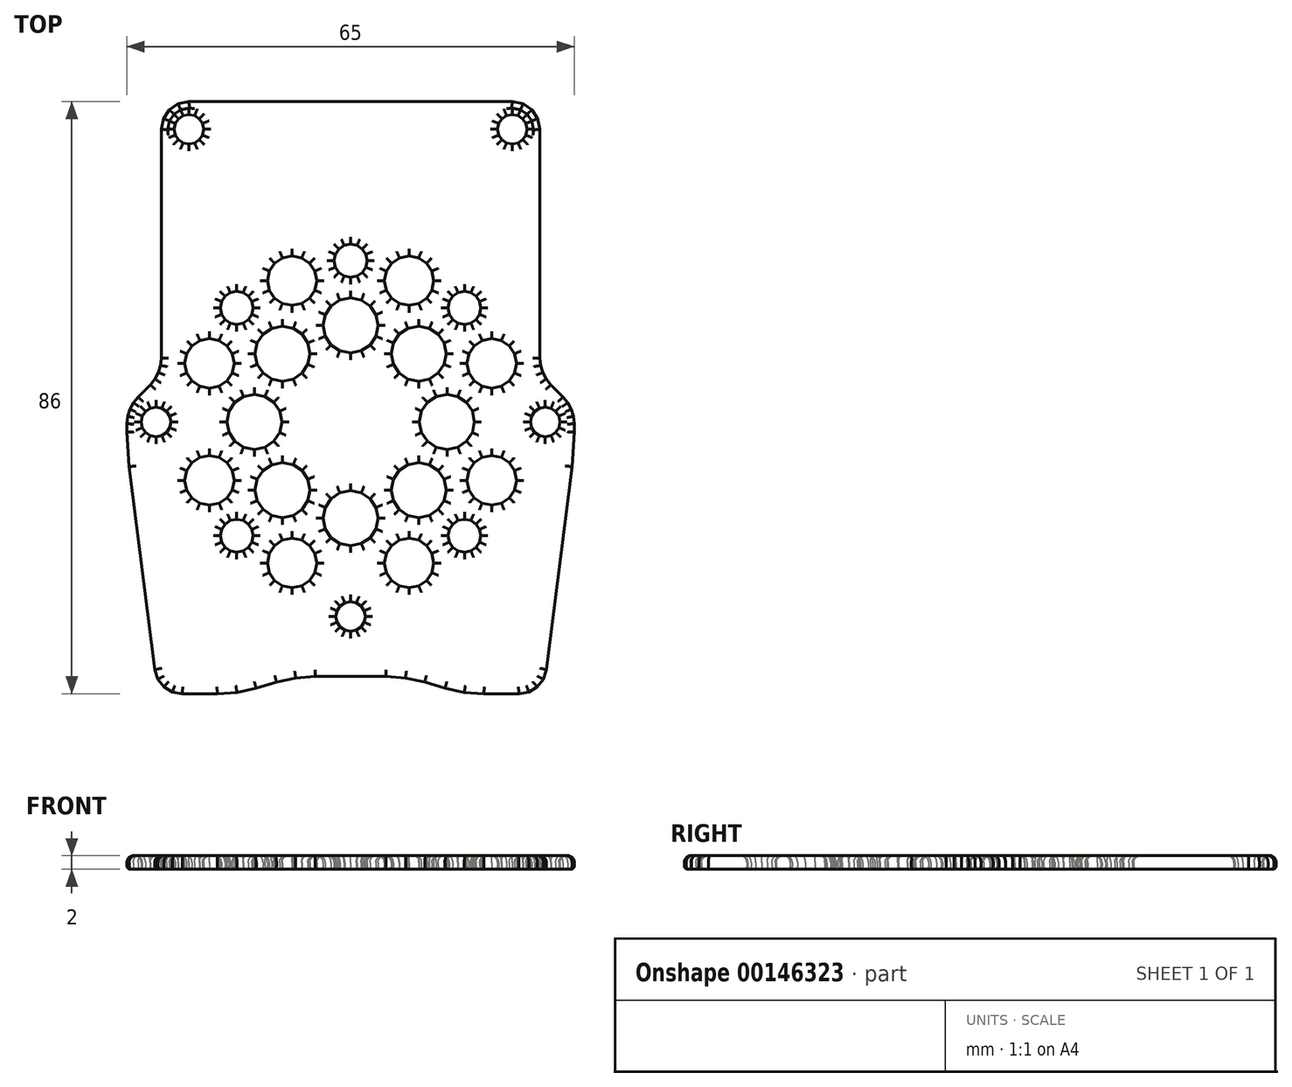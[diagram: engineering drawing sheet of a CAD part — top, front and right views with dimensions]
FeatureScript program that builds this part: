
annotation { "Feature Type Name" : "Feature", "Feature Type Description" : "" }
export const myFeature = defineFeature(function(context is Context, id is Id, definition is map)
    precondition{}
    {
        {
            var Q0;
            Q0=qCreatedBy(makeId("Top.planeOp"),FACE);
            var sketch = newSketch(context, id + "F0", { "sketchPlane" : qUnion([Q0])});
            skLineSegment(sketch, "E0", {"start": v(32.5, -1.28) * mm, "end": v(32.5, -2.48) * mm});
            skLineSegment(sketch, "E1", {"start": v(32.18, -7.5) * mm, "end": v(32.5, -2.48) * mm});
            skLineSegment(sketch, "E2", {"start": v(32.18, -7.5) * mm, "end": v(28.44, -37) * mm});
            skLineSegment(sketch, "E3", {"start": v(24.47, -40.5) * mm, "end": v(25.9, -40.23) * mm});
            skLineSegment(sketch, "E4", {"start": v(25.9, -40.23) * mm, "end": v(27.12, -39.5) * mm});
            skLineSegment(sketch, "E5", {"start": v(27.12, -39.5) * mm, "end": v(28, -38.4) * mm});
            skLineSegment(sketch, "E6", {"start": v(28, -38.4) * mm, "end": v(28.44, -37) * mm});
            skLineSegment(sketch, "E7", {"start": v(-10.76, -38.81) * mm, "end": v(-13.74, -39.69) * mm});
            skLineSegment(sketch, "E8", {"start": v(-19.38, -40.5) * mm, "end": v(-16.53, -40.3) * mm});
            skLineSegment(sketch, "E9", {"start": v(-16.53, -40.3) * mm, "end": v(-13.74, -39.69) * mm});
            skLineSegment(sketch, "E10", {"start": v(-19.38, -40.5) * mm, "end": v(-24.48, -40.5) * mm});
            skLineSegment(sketch, "E11", {"start": v(-5.12, -38) * mm, "end": v(-7.97, -38.2) * mm});
            skLineSegment(sketch, "E12", {"start": v(-7.97, -38.2) * mm, "end": v(-10.76, -38.81) * mm});
            skLineSegment(sketch, "E13", {"start": v(-5.12, -38) * mm, "end": v(5.12, -38) * mm});
            skLineSegment(sketch, "E14", {"start": v(10.76, -38.81) * mm, "end": v(7.97, -38.2) * mm});
            skLineSegment(sketch, "E15", {"start": v(7.97, -38.2) * mm, "end": v(5.12, -38) * mm});
            skLineSegment(sketch, "E16", {"start": v(10.76, -38.81) * mm, "end": v(13.74, -39.69) * mm});
            skLineSegment(sketch, "E17", {"start": v(13.74, -39.69) * mm, "end": v(16.53, -40.3) * mm});
            skLineSegment(sketch, "E18", {"start": v(16.53, -40.3) * mm, "end": v(19.38, -40.5) * mm});
            skLineSegment(sketch, "E19", {"start": v(19.38, -40.5) * mm, "end": v(24.47, -40.5) * mm});
            skLineSegment(sketch, "E20", {"start": v(-28.44, -37) * mm, "end": v(-28, -38.4) * mm});
            skLineSegment(sketch, "E21", {"start": v(-28, -38.4) * mm, "end": v(-27.12, -39.5) * mm});
            skLineSegment(sketch, "E22", {"start": v(-27.12, -39.5) * mm, "end": v(-25.91, -40.23) * mm});
            skLineSegment(sketch, "E23", {"start": v(-25.91, -40.23) * mm, "end": v(-24.48, -40.5) * mm});
            skLineSegment(sketch, "E24", {"start": v(-28.44, -37) * mm, "end": v(-32.18, -7.5) * mm});
            skLineSegment(sketch, "E25", {"start": v(-32.5, -2.48) * mm, "end": v(-32.18, -7.5) * mm});
            skLineSegment(sketch, "E26", {"start": v(-32.5, -2.48) * mm, "end": v(-32.5, -1.28) * mm});
            skLineSegment(sketch, "E27", {"start": v(-23.5, 45.5) * mm, "end": v(23.5, 45.5) * mm});
            skLineSegment(sketch, "E28", {"start": v(27.5, 41.5) * mm, "end": v(27.18, 43.06) * mm});
            skLineSegment(sketch, "E29", {"start": v(27.18, 43.06) * mm, "end": v(26.33, 44.33) * mm});
            skLineSegment(sketch, "E30", {"start": v(26.33, 44.33) * mm, "end": v(25.05, 45.19) * mm});
            skLineSegment(sketch, "E31", {"start": v(25.05, 45.19) * mm, "end": v(23.5, 45.5) * mm});
            skLineSegment(sketch, "E32", {"start": v(27.5, 41.5) * mm, "end": v(27.5, 8.28) * mm});
            skLineSegment(sketch, "E33", {"start": v(27.5, 8.28) * mm, "end": v(27.6, 7.2) * mm});
            skLineSegment(sketch, "E34", {"start": v(27.6, 7.2) * mm, "end": v(27.92, 6.17) * mm});
            skLineSegment(sketch, "E35", {"start": v(27.92, 6.17) * mm, "end": v(28.42, 5.23) * mm});
            skLineSegment(sketch, "E36", {"start": v(28.42, 5.23) * mm, "end": v(29.11, 4.39) * mm});
            skLineSegment(sketch, "E37", {"start": v(29.11, 4.39) * mm, "end": v(30.89, 2.61) * mm});
            skLineSegment(sketch, "E38", {"start": v(32.5, -1.28) * mm, "end": v(32.4, -0.2) * mm});
            skLineSegment(sketch, "E39", {"start": v(32.4, -0.2) * mm, "end": v(32.08, 0.83) * mm});
            skLineSegment(sketch, "E40", {"start": v(32.08, 0.83) * mm, "end": v(31.57, 1.77) * mm});
            skLineSegment(sketch, "E41", {"start": v(31.57, 1.77) * mm, "end": v(30.89, 2.61) * mm});
            skLineSegment(sketch, "E42", {"start": v(-30.89, 2.61) * mm, "end": v(-31.58, 1.77) * mm});
            skLineSegment(sketch, "E43", {"start": v(-31.58, 1.77) * mm, "end": v(-32.08, 0.83) * mm});
            skLineSegment(sketch, "E44", {"start": v(-32.08, 0.83) * mm, "end": v(-32.4, -0.2) * mm});
            skLineSegment(sketch, "E45", {"start": v(-32.4, -0.2) * mm, "end": v(-32.5, -1.28) * mm});
            skLineSegment(sketch, "E46", {"start": v(-30.89, 2.61) * mm, "end": v(-29.11, 4.39) * mm});
            skLineSegment(sketch, "E47", {"start": v(-29.11, 4.39) * mm, "end": v(-28.43, 5.23) * mm});
            skLineSegment(sketch, "E48", {"start": v(-28.43, 5.23) * mm, "end": v(-27.92, 6.17) * mm});
            skLineSegment(sketch, "E49", {"start": v(-27.92, 6.17) * mm, "end": v(-27.6, 7.2) * mm});
            skLineSegment(sketch, "E50", {"start": v(-27.6, 7.2) * mm, "end": v(-27.5, 8.28) * mm});
            skLineSegment(sketch, "E51", {"start": v(-27.5, 8.28) * mm, "end": v(-27.5, 41.5) * mm});
            skLineSegment(sketch, "E52", {"start": v(-23.5, 45.5) * mm, "end": v(-25.06, 45.19) * mm});
            skLineSegment(sketch, "E53", {"start": v(-25.06, 45.19) * mm, "end": v(-26.33, 44.33) * mm});
            skLineSegment(sketch, "E54", {"start": v(-26.33, 44.33) * mm, "end": v(-27.19, 43.06) * mm});
            skLineSegment(sketch, "E55", {"start": v(-27.19, 43.06) * mm, "end": v(-27.5, 41.5) * mm});
            skLineSegment(sketch, "E56", {"start": v(-26.13, -1) * mm, "end": v(-26.3, -0.16) * mm});
            skLineSegment(sketch, "E57", {"start": v(-26.3, -0.16) * mm, "end": v(-26.76, 0.52) * mm});
            skLineSegment(sketch, "E58", {"start": v(-26.76, 0.52) * mm, "end": v(-27.44, 0.98) * mm});
            skLineSegment(sketch, "E59", {"start": v(-27.44, 0.98) * mm, "end": v(-28.28, 1.15) * mm});
            skLineSegment(sketch, "E60", {"start": v(-28.28, 1.15) * mm, "end": v(-29.12, 0.98) * mm});
            skLineSegment(sketch, "E61", {"start": v(-29.12, 0.98) * mm, "end": v(-29.8, 0.52) * mm});
            skLineSegment(sketch, "E62", {"start": v(-29.8, 0.52) * mm, "end": v(-30.26, -0.16) * mm});
            skLineSegment(sketch, "E63", {"start": v(-30.26, -0.16) * mm, "end": v(-30.43, -1) * mm});
            skLineSegment(sketch, "E64", {"start": v(-30.43, -1) * mm, "end": v(-30.26, -1.83) * mm});
            skLineSegment(sketch, "E65", {"start": v(-30.26, -1.83) * mm, "end": v(-29.8, -2.52) * mm});
            skLineSegment(sketch, "E66", {"start": v(-29.8, -2.52) * mm, "end": v(-29.12, -2.98) * mm});
            skLineSegment(sketch, "E67", {"start": v(-29.12, -2.98) * mm, "end": v(-28.28, -3.15) * mm});
            skLineSegment(sketch, "E68", {"start": v(-28.28, -3.15) * mm, "end": v(-27.44, -2.98) * mm});
            skLineSegment(sketch, "E69", {"start": v(-27.44, -2.98) * mm, "end": v(-26.76, -2.52) * mm});
            skLineSegment(sketch, "E70", {"start": v(-26.76, -2.52) * mm, "end": v(-26.3, -1.83) * mm});
            skLineSegment(sketch, "E71", {"start": v(-26.3, -1.83) * mm, "end": v(-26.13, -1) * mm});
            skLineSegment(sketch, "E72", {"start": v(30.43, -1) * mm, "end": v(30.26, -0.16) * mm});
            skLineSegment(sketch, "E73", {"start": v(30.26, -0.16) * mm, "end": v(29.8, 0.52) * mm});
            skLineSegment(sketch, "E74", {"start": v(29.8, 0.52) * mm, "end": v(29.11, 0.98) * mm});
            skLineSegment(sketch, "E75", {"start": v(29.11, 0.98) * mm, "end": v(28.28, 1.15) * mm});
            skLineSegment(sketch, "E76", {"start": v(28.28, 1.15) * mm, "end": v(27.44, 0.98) * mm});
            skLineSegment(sketch, "E77", {"start": v(27.44, 0.98) * mm, "end": v(26.76, 0.52) * mm});
            skLineSegment(sketch, "E78", {"start": v(26.76, 0.52) * mm, "end": v(26.3, -0.16) * mm});
            skLineSegment(sketch, "E79", {"start": v(26.3, -0.16) * mm, "end": v(26.13, -1) * mm});
            skLineSegment(sketch, "E80", {"start": v(26.13, -1) * mm, "end": v(26.3, -1.83) * mm});
            skLineSegment(sketch, "E81", {"start": v(26.3, -1.83) * mm, "end": v(26.76, -2.52) * mm});
            skLineSegment(sketch, "E82", {"start": v(26.76, -2.52) * mm, "end": v(27.44, -2.98) * mm});
            skLineSegment(sketch, "E83", {"start": v(27.44, -2.98) * mm, "end": v(28.28, -3.15) * mm});
            skLineSegment(sketch, "E84", {"start": v(28.28, -3.15) * mm, "end": v(29.11, -2.98) * mm});
            skLineSegment(sketch, "E85", {"start": v(29.11, -2.98) * mm, "end": v(29.8, -2.52) * mm});
            skLineSegment(sketch, "E86", {"start": v(29.8, -2.52) * mm, "end": v(30.26, -1.83) * mm});
            skLineSegment(sketch, "E87", {"start": v(30.26, -1.83) * mm, "end": v(30.43, -1) * mm});
            skLineSegment(sketch, "E88", {"start": v(2.15, -29.28) * mm, "end": v(1.98, -28.44) * mm});
            skLineSegment(sketch, "E89", {"start": v(1.98, -28.44) * mm, "end": v(1.52, -27.76) * mm});
            skLineSegment(sketch, "E90", {"start": v(1.52, -27.76) * mm, "end": v(0.83, -27.3) * mm});
            skLineSegment(sketch, "E91", {"start": v(0.83, -27.3) * mm, "end": v(0, -27.13) * mm});
            skLineSegment(sketch, "E92", {"start": v(0, -27.13) * mm, "end": v(-0.84, -27.3) * mm});
            skLineSegment(sketch, "E93", {"start": v(-0.84, -27.3) * mm, "end": v(-1.52, -27.76) * mm});
            skLineSegment(sketch, "E94", {"start": v(-1.52, -27.76) * mm, "end": v(-1.98, -28.44) * mm});
            skLineSegment(sketch, "E95", {"start": v(-1.98, -28.44) * mm, "end": v(-2.15, -29.28) * mm});
            skLineSegment(sketch, "E96", {"start": v(-2.15, -29.28) * mm, "end": v(-1.98, -30.11) * mm});
            skLineSegment(sketch, "E97", {"start": v(-1.98, -30.11) * mm, "end": v(-1.52, -30.8) * mm});
            skLineSegment(sketch, "E98", {"start": v(-1.52, -30.8) * mm, "end": v(-0.84, -31.26) * mm});
            skLineSegment(sketch, "E99", {"start": v(-0.84, -31.26) * mm, "end": v(0, -31.43) * mm});
            skLineSegment(sketch, "E100", {"start": v(0, -31.43) * mm, "end": v(0.83, -31.26) * mm});
            skLineSegment(sketch, "E101", {"start": v(0.83, -31.26) * mm, "end": v(1.52, -30.8) * mm});
            skLineSegment(sketch, "E102", {"start": v(1.52, -30.8) * mm, "end": v(1.98, -30.11) * mm});
            skLineSegment(sketch, "E103", {"start": v(1.98, -30.11) * mm, "end": v(2.15, -29.28) * mm});
            skLineSegment(sketch, "E104", {"start": v(-21.35, 41.5) * mm, "end": v(-21.52, 42.34) * mm});
            skLineSegment(sketch, "E105", {"start": v(-21.52, 42.34) * mm, "end": v(-21.98, 43.02) * mm});
            skLineSegment(sketch, "E106", {"start": v(-21.98, 43.02) * mm, "end": v(-22.67, 43.48) * mm});
            skLineSegment(sketch, "E107", {"start": v(-22.67, 43.48) * mm, "end": v(-23.5, 43.65) * mm});
            skLineSegment(sketch, "E108", {"start": v(-23.5, 43.65) * mm, "end": v(-24.34, 43.48) * mm});
            skLineSegment(sketch, "E109", {"start": v(-24.34, 43.48) * mm, "end": v(-25.02, 43.02) * mm});
            skLineSegment(sketch, "E110", {"start": v(-25.02, 43.02) * mm, "end": v(-25.48, 42.34) * mm});
            skLineSegment(sketch, "E111", {"start": v(-25.48, 42.34) * mm, "end": v(-25.65, 41.5) * mm});
            skLineSegment(sketch, "E112", {"start": v(-25.65, 41.5) * mm, "end": v(-25.48, 40.67) * mm});
            skLineSegment(sketch, "E113", {"start": v(-25.48, 40.67) * mm, "end": v(-25.02, 39.98) * mm});
            skLineSegment(sketch, "E114", {"start": v(-25.02, 39.98) * mm, "end": v(-24.34, 39.52) * mm});
            skLineSegment(sketch, "E115", {"start": v(-24.34, 39.52) * mm, "end": v(-23.5, 39.35) * mm});
            skLineSegment(sketch, "E116", {"start": v(-23.5, 39.35) * mm, "end": v(-22.67, 39.52) * mm});
            skLineSegment(sketch, "E117", {"start": v(-22.67, 39.52) * mm, "end": v(-21.98, 39.98) * mm});
            skLineSegment(sketch, "E118", {"start": v(-21.98, 39.98) * mm, "end": v(-21.52, 40.67) * mm});
            skLineSegment(sketch, "E119", {"start": v(-21.52, 40.67) * mm, "end": v(-21.35, 41.5) * mm});
            skLineSegment(sketch, "E120", {"start": v(25.65, 41.5) * mm, "end": v(25.48, 42.34) * mm});
            skLineSegment(sketch, "E121", {"start": v(25.48, 42.34) * mm, "end": v(25.02, 43.02) * mm});
            skLineSegment(sketch, "E122", {"start": v(25.02, 43.02) * mm, "end": v(24.34, 43.48) * mm});
            skLineSegment(sketch, "E123", {"start": v(24.34, 43.48) * mm, "end": v(23.5, 43.65) * mm});
            skLineSegment(sketch, "E124", {"start": v(23.5, 43.65) * mm, "end": v(22.66, 43.48) * mm});
            skLineSegment(sketch, "E125", {"start": v(22.66, 43.48) * mm, "end": v(21.98, 43.02) * mm});
            skLineSegment(sketch, "E126", {"start": v(21.98, 43.02) * mm, "end": v(21.52, 42.34) * mm});
            skLineSegment(sketch, "E127", {"start": v(21.52, 42.34) * mm, "end": v(21.35, 41.5) * mm});
            skLineSegment(sketch, "E128", {"start": v(21.35, 41.5) * mm, "end": v(21.52, 40.67) * mm});
            skLineSegment(sketch, "E129", {"start": v(21.52, 40.67) * mm, "end": v(21.98, 39.98) * mm});
            skLineSegment(sketch, "E130", {"start": v(21.98, 39.98) * mm, "end": v(22.66, 39.52) * mm});
            skLineSegment(sketch, "E131", {"start": v(22.66, 39.52) * mm, "end": v(23.5, 39.35) * mm});
            skLineSegment(sketch, "E132", {"start": v(23.5, 39.35) * mm, "end": v(24.34, 39.52) * mm});
            skLineSegment(sketch, "E133", {"start": v(24.34, 39.52) * mm, "end": v(25.02, 39.98) * mm});
            skLineSegment(sketch, "E134", {"start": v(25.02, 39.98) * mm, "end": v(25.48, 40.67) * mm});
            skLineSegment(sketch, "E135", {"start": v(25.48, 40.67) * mm, "end": v(25.65, 41.5) * mm});
            skLineSegment(sketch, "E136", {"start": v(2.4, 22.4) * mm, "end": v(2.2, 23.33) * mm});
            skLineSegment(sketch, "E137", {"start": v(2.2, 23.33) * mm, "end": v(1.7, 24.1) * mm});
            skLineSegment(sketch, "E138", {"start": v(1.7, 24.1) * mm, "end": v(0.93, 24.61) * mm});
            skLineSegment(sketch, "E139", {"start": v(0.93, 24.61) * mm, "end": v(0, 24.8) * mm});
            skLineSegment(sketch, "E140", {"start": v(0, 24.8) * mm, "end": v(-0.93, 24.61) * mm});
            skLineSegment(sketch, "E141", {"start": v(-0.93, 24.61) * mm, "end": v(-1.7, 24.1) * mm});
            skLineSegment(sketch, "E142", {"start": v(-1.7, 24.1) * mm, "end": v(-2.21, 23.33) * mm});
            skLineSegment(sketch, "E143", {"start": v(-2.21, 23.33) * mm, "end": v(-2.4, 22.4) * mm});
            skLineSegment(sketch, "E144", {"start": v(-2.4, 22.4) * mm, "end": v(-2.21, 21.47) * mm});
            skLineSegment(sketch, "E145", {"start": v(-2.21, 21.47) * mm, "end": v(-1.7, 20.7) * mm});
            skLineSegment(sketch, "E146", {"start": v(-1.7, 20.7) * mm, "end": v(-0.93, 20.19) * mm});
            skLineSegment(sketch, "E147", {"start": v(-0.93, 20.19) * mm, "end": v(0, 20) * mm});
            skLineSegment(sketch, "E148", {"start": v(0, 20) * mm, "end": v(0.93, 20.19) * mm});
            skLineSegment(sketch, "E149", {"start": v(0.93, 20.19) * mm, "end": v(1.7, 20.7) * mm});
            skLineSegment(sketch, "E150", {"start": v(1.7, 20.7) * mm, "end": v(2.2, 21.47) * mm});
            skLineSegment(sketch, "E151", {"start": v(2.2, 21.47) * mm, "end": v(2.4, 22.4) * mm});
            skLineSegment(sketch, "E152", {"start": v(4, 13) * mm, "end": v(3.68, 14.56) * mm});
            skLineSegment(sketch, "E153", {"start": v(3.68, 14.56) * mm, "end": v(2.83, 15.83) * mm});
            skLineSegment(sketch, "E154", {"start": v(2.83, 15.83) * mm, "end": v(1.56, 16.69) * mm});
            skLineSegment(sketch, "E155", {"start": v(1.56, 16.69) * mm, "end": v(0, 17) * mm});
            skLineSegment(sketch, "E156", {"start": v(0, 17) * mm, "end": v(-1.56, 16.69) * mm});
            skLineSegment(sketch, "E157", {"start": v(-1.56, 16.69) * mm, "end": v(-2.83, 15.83) * mm});
            skLineSegment(sketch, "E158", {"start": v(-2.83, 15.83) * mm, "end": v(-3.69, 14.56) * mm});
            skLineSegment(sketch, "E159", {"start": v(-3.69, 14.56) * mm, "end": v(-4, 13) * mm});
            skLineSegment(sketch, "E160", {"start": v(-4, 13) * mm, "end": v(-3.69, 11.44) * mm});
            skLineSegment(sketch, "E161", {"start": v(-3.69, 11.44) * mm, "end": v(-2.83, 10.17) * mm});
            skLineSegment(sketch, "E162", {"start": v(-2.83, 10.17) * mm, "end": v(-1.56, 9.31) * mm});
            skLineSegment(sketch, "E163", {"start": v(-1.56, 9.31) * mm, "end": v(0, 9) * mm});
            skLineSegment(sketch, "E164", {"start": v(0, 9) * mm, "end": v(1.56, 9.31) * mm});
            skLineSegment(sketch, "E165", {"start": v(1.56, 9.31) * mm, "end": v(2.83, 10.17) * mm});
            skLineSegment(sketch, "E166", {"start": v(2.83, 10.17) * mm, "end": v(3.68, 11.44) * mm});
            skLineSegment(sketch, "E167", {"start": v(3.68, 11.44) * mm, "end": v(4, 13) * mm});
            skLineSegment(sketch, "E168", {"start": v(-4.9, 19.5) * mm, "end": v(-5.18, 20.91) * mm});
            skLineSegment(sketch, "E169", {"start": v(-5.18, 20.91) * mm, "end": v(-5.95, 22.06) * mm});
            skLineSegment(sketch, "E170", {"start": v(-5.95, 22.06) * mm, "end": v(-7.1, 22.83) * mm});
            skLineSegment(sketch, "E171", {"start": v(-7.1, 22.83) * mm, "end": v(-8.5, 23.11) * mm});
            skLineSegment(sketch, "E172", {"start": v(-8.5, 23.11) * mm, "end": v(-9.9, 22.83) * mm});
            skLineSegment(sketch, "E173", {"start": v(-9.9, 22.83) * mm, "end": v(-11.04, 22.06) * mm});
            skLineSegment(sketch, "E174", {"start": v(-11.04, 22.06) * mm, "end": v(-11.81, 20.91) * mm});
            skLineSegment(sketch, "E175", {"start": v(-11.81, 20.91) * mm, "end": v(-12.1, 19.5) * mm});
            skLineSegment(sketch, "E176", {"start": v(-12.1, 19.5) * mm, "end": v(-11.81, 18.1) * mm});
            skLineSegment(sketch, "E177", {"start": v(-11.81, 18.1) * mm, "end": v(-11.04, 16.97) * mm});
            skLineSegment(sketch, "E178", {"start": v(-11.04, 16.97) * mm, "end": v(-9.9, 16.2) * mm});
            skLineSegment(sketch, "E179", {"start": v(-9.9, 16.2) * mm, "end": v(-8.5, 15.91) * mm});
            skLineSegment(sketch, "E180", {"start": v(-8.5, 15.91) * mm, "end": v(-7.1, 16.2) * mm});
            skLineSegment(sketch, "E181", {"start": v(-7.1, 16.2) * mm, "end": v(-5.95, 16.97) * mm});
            skLineSegment(sketch, "E182", {"start": v(-5.95, 16.97) * mm, "end": v(-5.18, 18.1) * mm});
            skLineSegment(sketch, "E183", {"start": v(-5.18, 18.1) * mm, "end": v(-4.9, 19.5) * mm});
            skLineSegment(sketch, "E184", {"start": v(4, -15) * mm, "end": v(3.68, -13.44) * mm});
            skLineSegment(sketch, "E185", {"start": v(3.68, -13.44) * mm, "end": v(2.83, -12.17) * mm});
            skLineSegment(sketch, "E186", {"start": v(2.83, -12.17) * mm, "end": v(1.56, -11.31) * mm});
            skLineSegment(sketch, "E187", {"start": v(1.56, -11.31) * mm, "end": v(0, -11) * mm});
            skLineSegment(sketch, "E188", {"start": v(0, -11) * mm, "end": v(-1.56, -11.31) * mm});
            skLineSegment(sketch, "E189", {"start": v(-1.56, -11.31) * mm, "end": v(-2.83, -12.17) * mm});
            skLineSegment(sketch, "E190", {"start": v(-2.83, -12.17) * mm, "end": v(-3.69, -13.44) * mm});
            skLineSegment(sketch, "E191", {"start": v(-3.69, -13.44) * mm, "end": v(-4, -15) * mm});
            skLineSegment(sketch, "E192", {"start": v(-4, -15) * mm, "end": v(-3.69, -16.56) * mm});
            skLineSegment(sketch, "E193", {"start": v(-3.69, -16.56) * mm, "end": v(-2.83, -17.83) * mm});
            skLineSegment(sketch, "E194", {"start": v(-2.83, -17.83) * mm, "end": v(-1.56, -18.68) * mm});
            skLineSegment(sketch, "E195", {"start": v(-1.56, -18.68) * mm, "end": v(0, -19) * mm});
            skLineSegment(sketch, "E196", {"start": v(0, -19) * mm, "end": v(1.56, -18.68) * mm});
            skLineSegment(sketch, "E197", {"start": v(1.56, -18.68) * mm, "end": v(2.83, -17.83) * mm});
            skLineSegment(sketch, "E198", {"start": v(2.83, -17.83) * mm, "end": v(3.68, -16.56) * mm});
            skLineSegment(sketch, "E199", {"start": v(3.68, -16.56) * mm, "end": v(4, -15) * mm});
            skLineSegment(sketch, "E200", {"start": v(12.1, -21.51) * mm, "end": v(11.81, -20.1) * mm});
            skLineSegment(sketch, "E201", {"start": v(11.81, -20.1) * mm, "end": v(11.04, -18.96) * mm});
            skLineSegment(sketch, "E202", {"start": v(11.04, -18.96) * mm, "end": v(9.9, -18.2) * mm});
            skLineSegment(sketch, "E203", {"start": v(9.9, -18.2) * mm, "end": v(8.5, -17.9) * mm});
            skLineSegment(sketch, "E204", {"start": v(8.5, -17.9) * mm, "end": v(7.1, -18.2) * mm});
            skLineSegment(sketch, "E205", {"start": v(7.1, -18.2) * mm, "end": v(5.95, -18.96) * mm});
            skLineSegment(sketch, "E206", {"start": v(5.95, -18.96) * mm, "end": v(5.18, -20.1) * mm});
            skLineSegment(sketch, "E207", {"start": v(5.18, -20.1) * mm, "end": v(4.9, -21.51) * mm});
            skLineSegment(sketch, "E208", {"start": v(4.9, -21.51) * mm, "end": v(5.18, -22.91) * mm});
            skLineSegment(sketch, "E209", {"start": v(5.18, -22.91) * mm, "end": v(5.95, -24.05) * mm});
            skLineSegment(sketch, "E210", {"start": v(5.95, -24.05) * mm, "end": v(7.1, -24.83) * mm});
            skLineSegment(sketch, "E211", {"start": v(7.1, -24.83) * mm, "end": v(8.5, -25.1) * mm});
            skLineSegment(sketch, "E212", {"start": v(8.5, -25.1) * mm, "end": v(9.9, -24.83) * mm});
            skLineSegment(sketch, "E213", {"start": v(9.9, -24.83) * mm, "end": v(11.04, -24.05) * mm});
            skLineSegment(sketch, "E214", {"start": v(11.04, -24.05) * mm, "end": v(11.81, -22.91) * mm});
            skLineSegment(sketch, "E215", {"start": v(11.81, -22.91) * mm, "end": v(12.1, -21.51) * mm});
            skLineSegment(sketch, "E216", {"start": v(-10, -1) * mm, "end": v(-10.32, 0.56) * mm});
            skLineSegment(sketch, "E217", {"start": v(-10.32, 0.56) * mm, "end": v(-11.17, 1.83) * mm});
            skLineSegment(sketch, "E218", {"start": v(-11.17, 1.83) * mm, "end": v(-12.44, 2.69) * mm});
            skLineSegment(sketch, "E219", {"start": v(-12.44, 2.69) * mm, "end": v(-14, 3) * mm});
            skLineSegment(sketch, "E220", {"start": v(-14, 3) * mm, "end": v(-15.56, 2.69) * mm});
            skLineSegment(sketch, "E221", {"start": v(-15.56, 2.69) * mm, "end": v(-16.83, 1.83) * mm});
            skLineSegment(sketch, "E222", {"start": v(-16.83, 1.83) * mm, "end": v(-17.69, 0.56) * mm});
            skLineSegment(sketch, "E223", {"start": v(-17.69, 0.56) * mm, "end": v(-18, -1) * mm});
            skLineSegment(sketch, "E224", {"start": v(-18, -1) * mm, "end": v(-17.69, -2.56) * mm});
            skLineSegment(sketch, "E225", {"start": v(-17.69, -2.56) * mm, "end": v(-16.83, -3.83) * mm});
            skLineSegment(sketch, "E226", {"start": v(-16.83, -3.83) * mm, "end": v(-15.56, -4.68) * mm});
            skLineSegment(sketch, "E227", {"start": v(-15.56, -4.68) * mm, "end": v(-14, -5) * mm});
            skLineSegment(sketch, "E228", {"start": v(-14, -5) * mm, "end": v(-12.44, -4.68) * mm});
            skLineSegment(sketch, "E229", {"start": v(-12.44, -4.68) * mm, "end": v(-11.17, -3.83) * mm});
            skLineSegment(sketch, "E230", {"start": v(-11.17, -3.83) * mm, "end": v(-10.32, -2.56) * mm});
            skLineSegment(sketch, "E231", {"start": v(-10.32, -2.56) * mm, "end": v(-10, -1) * mm});
            skLineSegment(sketch, "E232", {"start": v(-16.91, -9.5) * mm, "end": v(-17.2, -8.1) * mm});
            skLineSegment(sketch, "E233", {"start": v(-17.2, -8.1) * mm, "end": v(-17.97, -6.95) * mm});
            skLineSegment(sketch, "E234", {"start": v(-17.97, -6.95) * mm, "end": v(-19.1, -6.18) * mm});
            skLineSegment(sketch, "E235", {"start": v(-19.1, -6.18) * mm, "end": v(-20.5, -5.9) * mm});
            skLineSegment(sketch, "E236", {"start": v(-20.5, -5.9) * mm, "end": v(-21.91, -6.18) * mm});
            skLineSegment(sketch, "E237", {"start": v(-21.91, -6.18) * mm, "end": v(-23.06, -6.95) * mm});
            skLineSegment(sketch, "E238", {"start": v(-23.06, -6.95) * mm, "end": v(-23.83, -8.1) * mm});
            skLineSegment(sketch, "E239", {"start": v(-23.83, -8.1) * mm, "end": v(-24.11, -9.5) * mm});
            skLineSegment(sketch, "E240", {"start": v(-24.11, -9.5) * mm, "end": v(-23.83, -10.9) * mm});
            skLineSegment(sketch, "E241", {"start": v(-23.83, -10.9) * mm, "end": v(-23.06, -12.04) * mm});
            skLineSegment(sketch, "E242", {"start": v(-23.06, -12.04) * mm, "end": v(-21.91, -12.81) * mm});
            skLineSegment(sketch, "E243", {"start": v(-21.91, -12.81) * mm, "end": v(-20.5, -13.1) * mm});
            skLineSegment(sketch, "E244", {"start": v(-20.5, -13.1) * mm, "end": v(-19.1, -12.81) * mm});
            skLineSegment(sketch, "E245", {"start": v(-19.1, -12.81) * mm, "end": v(-17.97, -12.04) * mm});
            skLineSegment(sketch, "E246", {"start": v(-17.97, -12.04) * mm, "end": v(-17.2, -10.9) * mm});
            skLineSegment(sketch, "E247", {"start": v(-17.2, -10.9) * mm, "end": v(-16.91, -9.5) * mm});
            skLineSegment(sketch, "E248", {"start": v(18, -1) * mm, "end": v(17.68, 0.56) * mm});
            skLineSegment(sketch, "E249", {"start": v(17.68, 0.56) * mm, "end": v(16.83, 1.83) * mm});
            skLineSegment(sketch, "E250", {"start": v(16.83, 1.83) * mm, "end": v(15.56, 2.69) * mm});
            skLineSegment(sketch, "E251", {"start": v(15.56, 2.69) * mm, "end": v(14, 3) * mm});
            skLineSegment(sketch, "E252", {"start": v(14, 3) * mm, "end": v(12.44, 2.69) * mm});
            skLineSegment(sketch, "E253", {"start": v(12.44, 2.69) * mm, "end": v(11.17, 1.83) * mm});
            skLineSegment(sketch, "E254", {"start": v(11.17, 1.83) * mm, "end": v(10.31, 0.56) * mm});
            skLineSegment(sketch, "E255", {"start": v(10.31, 0.56) * mm, "end": v(10, -1) * mm});
            skLineSegment(sketch, "E256", {"start": v(10, -1) * mm, "end": v(10.31, -2.56) * mm});
            skLineSegment(sketch, "E257", {"start": v(10.31, -2.56) * mm, "end": v(11.17, -3.83) * mm});
            skLineSegment(sketch, "E258", {"start": v(11.17, -3.83) * mm, "end": v(12.44, -4.68) * mm});
            skLineSegment(sketch, "E259", {"start": v(12.44, -4.68) * mm, "end": v(14, -5) * mm});
            skLineSegment(sketch, "E260", {"start": v(14, -5) * mm, "end": v(15.56, -4.68) * mm});
            skLineSegment(sketch, "E261", {"start": v(15.56, -4.68) * mm, "end": v(16.83, -3.83) * mm});
            skLineSegment(sketch, "E262", {"start": v(16.83, -3.83) * mm, "end": v(17.68, -2.56) * mm});
            skLineSegment(sketch, "E263", {"start": v(17.68, -2.56) * mm, "end": v(18, -1) * mm});
            skLineSegment(sketch, "E264", {"start": v(24.1, 7.5) * mm, "end": v(23.83, 8.9) * mm});
            skLineSegment(sketch, "E265", {"start": v(23.83, 8.9) * mm, "end": v(23.05, 10.04) * mm});
            skLineSegment(sketch, "E266", {"start": v(23.05, 10.04) * mm, "end": v(21.91, 10.81) * mm});
            skLineSegment(sketch, "E267", {"start": v(21.91, 10.81) * mm, "end": v(20.5, 11.1) * mm});
            skLineSegment(sketch, "E268", {"start": v(20.5, 11.1) * mm, "end": v(19.1, 10.81) * mm});
            skLineSegment(sketch, "E269", {"start": v(19.1, 10.81) * mm, "end": v(17.96, 10.04) * mm});
            skLineSegment(sketch, "E270", {"start": v(17.96, 10.04) * mm, "end": v(17.2, 8.9) * mm});
            skLineSegment(sketch, "E271", {"start": v(17.2, 8.9) * mm, "end": v(16.9, 7.5) * mm});
            skLineSegment(sketch, "E272", {"start": v(16.9, 7.5) * mm, "end": v(17.2, 6.1) * mm});
            skLineSegment(sketch, "E273", {"start": v(17.2, 6.1) * mm, "end": v(17.96, 4.95) * mm});
            skLineSegment(sketch, "E274", {"start": v(17.96, 4.95) * mm, "end": v(19.1, 4.18) * mm});
            skLineSegment(sketch, "E275", {"start": v(19.1, 4.18) * mm, "end": v(20.5, 3.9) * mm});
            skLineSegment(sketch, "E276", {"start": v(20.5, 3.9) * mm, "end": v(21.91, 4.18) * mm});
            skLineSegment(sketch, "E277", {"start": v(21.91, 4.18) * mm, "end": v(23.05, 4.95) * mm});
            skLineSegment(sketch, "E278", {"start": v(23.05, 4.95) * mm, "end": v(23.83, 6.1) * mm});
            skLineSegment(sketch, "E279", {"start": v(23.83, 6.1) * mm, "end": v(24.1, 7.5) * mm});
            skLineSegment(sketch, "E280", {"start": v(-14.15, 15.55) * mm, "end": v(-14.34, 16.48) * mm});
            skLineSegment(sketch, "E281", {"start": v(-14.34, 16.48) * mm, "end": v(-14.85, 17.24) * mm});
            skLineSegment(sketch, "E282", {"start": v(-14.85, 17.24) * mm, "end": v(-15.61, 17.76) * mm});
            skLineSegment(sketch, "E283", {"start": v(-15.61, 17.76) * mm, "end": v(-16.55, 17.95) * mm});
            skLineSegment(sketch, "E284", {"start": v(-16.55, 17.95) * mm, "end": v(-17.48, 17.76) * mm});
            skLineSegment(sketch, "E285", {"start": v(-17.48, 17.76) * mm, "end": v(-18.24, 17.24) * mm});
            skLineSegment(sketch, "E286", {"start": v(-18.24, 17.24) * mm, "end": v(-18.76, 16.48) * mm});
            skLineSegment(sketch, "E287", {"start": v(-18.76, 16.48) * mm, "end": v(-18.95, 15.55) * mm});
            skLineSegment(sketch, "E288", {"start": v(-18.95, 15.55) * mm, "end": v(-18.76, 14.61) * mm});
            skLineSegment(sketch, "E289", {"start": v(-18.76, 14.61) * mm, "end": v(-18.24, 13.85) * mm});
            skLineSegment(sketch, "E290", {"start": v(-18.24, 13.85) * mm, "end": v(-17.48, 13.34) * mm});
            skLineSegment(sketch, "E291", {"start": v(-17.48, 13.34) * mm, "end": v(-16.55, 13.15) * mm});
            skLineSegment(sketch, "E292", {"start": v(-16.55, 13.15) * mm, "end": v(-15.61, 13.34) * mm});
            skLineSegment(sketch, "E293", {"start": v(-15.61, 13.34) * mm, "end": v(-14.85, 13.85) * mm});
            skLineSegment(sketch, "E294", {"start": v(-14.85, 13.85) * mm, "end": v(-14.34, 14.61) * mm});
            skLineSegment(sketch, "E295", {"start": v(-14.34, 14.61) * mm, "end": v(-14.15, 15.55) * mm});
            skLineSegment(sketch, "E296", {"start": v(-5.9, 8.9) * mm, "end": v(-6.22, 10.46) * mm});
            skLineSegment(sketch, "E297", {"start": v(-6.22, 10.46) * mm, "end": v(-7.07, 11.73) * mm});
            skLineSegment(sketch, "E298", {"start": v(-7.07, 11.73) * mm, "end": v(-8.34, 12.58) * mm});
            skLineSegment(sketch, "E299", {"start": v(-8.34, 12.58) * mm, "end": v(-9.9, 12.9) * mm});
            skLineSegment(sketch, "E300", {"start": v(-9.9, 12.9) * mm, "end": v(-11.46, 12.58) * mm});
            skLineSegment(sketch, "E301", {"start": v(-11.46, 12.58) * mm, "end": v(-12.73, 11.73) * mm});
            skLineSegment(sketch, "E302", {"start": v(-12.73, 11.73) * mm, "end": v(-13.59, 10.46) * mm});
            skLineSegment(sketch, "E303", {"start": v(-13.59, 10.46) * mm, "end": v(-13.9, 8.9) * mm});
            skLineSegment(sketch, "E304", {"start": v(-13.9, 8.9) * mm, "end": v(-13.59, 7.34) * mm});
            skLineSegment(sketch, "E305", {"start": v(-13.59, 7.34) * mm, "end": v(-12.73, 6.07) * mm});
            skLineSegment(sketch, "E306", {"start": v(-12.73, 6.07) * mm, "end": v(-11.46, 5.21) * mm});
            skLineSegment(sketch, "E307", {"start": v(-11.46, 5.21) * mm, "end": v(-9.9, 4.9) * mm});
            skLineSegment(sketch, "E308", {"start": v(-9.9, 4.9) * mm, "end": v(-8.34, 5.21) * mm});
            skLineSegment(sketch, "E309", {"start": v(-8.34, 5.21) * mm, "end": v(-7.07, 6.07) * mm});
            skLineSegment(sketch, "E310", {"start": v(-7.07, 6.07) * mm, "end": v(-6.22, 7.34) * mm});
            skLineSegment(sketch, "E311", {"start": v(-6.22, 7.34) * mm, "end": v(-5.9, 8.9) * mm});
            skLineSegment(sketch, "E312", {"start": v(-16.91, 7.5) * mm, "end": v(-17.2, 8.9) * mm});
            skLineSegment(sketch, "E313", {"start": v(-17.2, 8.9) * mm, "end": v(-17.97, 10.04) * mm});
            skLineSegment(sketch, "E314", {"start": v(-17.97, 10.04) * mm, "end": v(-19.1, 10.81) * mm});
            skLineSegment(sketch, "E315", {"start": v(-19.1, 10.81) * mm, "end": v(-20.5, 11.1) * mm});
            skLineSegment(sketch, "E316", {"start": v(-20.5, 11.1) * mm, "end": v(-21.91, 10.81) * mm});
            skLineSegment(sketch, "E317", {"start": v(-21.91, 10.81) * mm, "end": v(-23.06, 10.04) * mm});
            skLineSegment(sketch, "E318", {"start": v(-23.06, 10.04) * mm, "end": v(-23.83, 8.9) * mm});
            skLineSegment(sketch, "E319", {"start": v(-23.83, 8.9) * mm, "end": v(-24.11, 7.5) * mm});
            skLineSegment(sketch, "E320", {"start": v(-24.11, 7.5) * mm, "end": v(-23.83, 6.1) * mm});
            skLineSegment(sketch, "E321", {"start": v(-23.83, 6.1) * mm, "end": v(-23.06, 4.95) * mm});
            skLineSegment(sketch, "E322", {"start": v(-23.06, 4.95) * mm, "end": v(-21.91, 4.18) * mm});
            skLineSegment(sketch, "E323", {"start": v(-21.91, 4.18) * mm, "end": v(-20.5, 3.9) * mm});
            skLineSegment(sketch, "E324", {"start": v(-20.5, 3.9) * mm, "end": v(-19.1, 4.18) * mm});
            skLineSegment(sketch, "E325", {"start": v(-19.1, 4.18) * mm, "end": v(-17.97, 4.95) * mm});
            skLineSegment(sketch, "E326", {"start": v(-17.97, 4.95) * mm, "end": v(-17.2, 6.1) * mm});
            skLineSegment(sketch, "E327", {"start": v(-17.2, 6.1) * mm, "end": v(-16.91, 7.5) * mm});
            skLineSegment(sketch, "E328", {"start": v(18.95, -17.55) * mm, "end": v(18.76, -16.61) * mm});
            skLineSegment(sketch, "E329", {"start": v(18.76, -16.61) * mm, "end": v(18.24, -15.85) * mm});
            skLineSegment(sketch, "E330", {"start": v(18.24, -15.85) * mm, "end": v(17.48, -15.33) * mm});
            skLineSegment(sketch, "E331", {"start": v(17.48, -15.33) * mm, "end": v(16.55, -15.15) * mm});
            skLineSegment(sketch, "E332", {"start": v(16.55, -15.15) * mm, "end": v(15.61, -15.33) * mm});
            skLineSegment(sketch, "E333", {"start": v(15.61, -15.33) * mm, "end": v(14.85, -15.85) * mm});
            skLineSegment(sketch, "E334", {"start": v(14.85, -15.85) * mm, "end": v(14.33, -16.61) * mm});
            skLineSegment(sketch, "E335", {"start": v(14.33, -16.61) * mm, "end": v(14.15, -17.55) * mm});
            skLineSegment(sketch, "E336", {"start": v(14.15, -17.55) * mm, "end": v(14.33, -18.48) * mm});
            skLineSegment(sketch, "E337", {"start": v(14.33, -18.48) * mm, "end": v(14.85, -19.24) * mm});
            skLineSegment(sketch, "E338", {"start": v(14.85, -19.24) * mm, "end": v(15.61, -19.76) * mm});
            skLineSegment(sketch, "E339", {"start": v(15.61, -19.76) * mm, "end": v(16.55, -19.95) * mm});
            skLineSegment(sketch, "E340", {"start": v(16.55, -19.95) * mm, "end": v(17.48, -19.76) * mm});
            skLineSegment(sketch, "E341", {"start": v(17.48, -19.76) * mm, "end": v(18.24, -19.24) * mm});
            skLineSegment(sketch, "E342", {"start": v(18.24, -19.24) * mm, "end": v(18.76, -18.48) * mm});
            skLineSegment(sketch, "E343", {"start": v(18.76, -18.48) * mm, "end": v(18.95, -17.55) * mm});
            skLineSegment(sketch, "E344", {"start": v(13.9, -10.9) * mm, "end": v(13.58, -9.34) * mm});
            skLineSegment(sketch, "E345", {"start": v(13.58, -9.34) * mm, "end": v(12.73, -8.07) * mm});
            skLineSegment(sketch, "E346", {"start": v(12.73, -8.07) * mm, "end": v(11.45, -7.21) * mm});
            skLineSegment(sketch, "E347", {"start": v(11.45, -7.21) * mm, "end": v(9.9, -6.9) * mm});
            skLineSegment(sketch, "E348", {"start": v(9.9, -6.9) * mm, "end": v(8.34, -7.21) * mm});
            skLineSegment(sketch, "E349", {"start": v(8.34, -7.21) * mm, "end": v(7.07, -8.07) * mm});
            skLineSegment(sketch, "E350", {"start": v(7.07, -8.07) * mm, "end": v(6.21, -9.34) * mm});
            skLineSegment(sketch, "E351", {"start": v(6.21, -9.34) * mm, "end": v(5.9, -10.9) * mm});
            skLineSegment(sketch, "E352", {"start": v(5.9, -10.9) * mm, "end": v(6.21, -12.46) * mm});
            skLineSegment(sketch, "E353", {"start": v(6.21, -12.46) * mm, "end": v(7.07, -13.73) * mm});
            skLineSegment(sketch, "E354", {"start": v(7.07, -13.73) * mm, "end": v(8.34, -14.58) * mm});
            skLineSegment(sketch, "E355", {"start": v(8.34, -14.58) * mm, "end": v(9.9, -14.9) * mm});
            skLineSegment(sketch, "E356", {"start": v(9.9, -14.9) * mm, "end": v(11.45, -14.58) * mm});
            skLineSegment(sketch, "E357", {"start": v(11.45, -14.58) * mm, "end": v(12.73, -13.73) * mm});
            skLineSegment(sketch, "E358", {"start": v(12.73, -13.73) * mm, "end": v(13.58, -12.46) * mm});
            skLineSegment(sketch, "E359", {"start": v(13.58, -12.46) * mm, "end": v(13.9, -10.9) * mm});
            skLineSegment(sketch, "E360", {"start": v(24.1, -9.5) * mm, "end": v(23.83, -8.1) * mm});
            skLineSegment(sketch, "E361", {"start": v(23.83, -8.1) * mm, "end": v(23.05, -6.95) * mm});
            skLineSegment(sketch, "E362", {"start": v(23.05, -6.95) * mm, "end": v(21.91, -6.18) * mm});
            skLineSegment(sketch, "E363", {"start": v(21.91, -6.18) * mm, "end": v(20.5, -5.9) * mm});
            skLineSegment(sketch, "E364", {"start": v(20.5, -5.9) * mm, "end": v(19.1, -6.18) * mm});
            skLineSegment(sketch, "E365", {"start": v(19.1, -6.18) * mm, "end": v(17.96, -6.95) * mm});
            skLineSegment(sketch, "E366", {"start": v(17.96, -6.95) * mm, "end": v(17.2, -8.1) * mm});
            skLineSegment(sketch, "E367", {"start": v(17.2, -8.1) * mm, "end": v(16.9, -9.5) * mm});
            skLineSegment(sketch, "E368", {"start": v(16.9, -9.5) * mm, "end": v(17.2, -10.9) * mm});
            skLineSegment(sketch, "E369", {"start": v(17.2, -10.9) * mm, "end": v(17.96, -12.04) * mm});
            skLineSegment(sketch, "E370", {"start": v(17.96, -12.04) * mm, "end": v(19.1, -12.81) * mm});
            skLineSegment(sketch, "E371", {"start": v(19.1, -12.81) * mm, "end": v(20.5, -13.1) * mm});
            skLineSegment(sketch, "E372", {"start": v(20.5, -13.1) * mm, "end": v(21.91, -12.81) * mm});
            skLineSegment(sketch, "E373", {"start": v(21.91, -12.81) * mm, "end": v(23.05, -12.04) * mm});
            skLineSegment(sketch, "E374", {"start": v(23.05, -12.04) * mm, "end": v(23.83, -10.9) * mm});
            skLineSegment(sketch, "E375", {"start": v(23.83, -10.9) * mm, "end": v(24.1, -9.5) * mm});
            skLineSegment(sketch, "E376", {"start": v(-14.15, -17.55) * mm, "end": v(-14.34, -16.61) * mm});
            skLineSegment(sketch, "E377", {"start": v(-14.34, -16.61) * mm, "end": v(-14.85, -15.85) * mm});
            skLineSegment(sketch, "E378", {"start": v(-14.85, -15.85) * mm, "end": v(-15.61, -15.33) * mm});
            skLineSegment(sketch, "E379", {"start": v(-15.61, -15.33) * mm, "end": v(-16.55, -15.15) * mm});
            skLineSegment(sketch, "E380", {"start": v(-16.55, -15.15) * mm, "end": v(-17.48, -15.33) * mm});
            skLineSegment(sketch, "E381", {"start": v(-17.48, -15.33) * mm, "end": v(-18.24, -15.85) * mm});
            skLineSegment(sketch, "E382", {"start": v(-18.24, -15.85) * mm, "end": v(-18.76, -16.61) * mm});
            skLineSegment(sketch, "E383", {"start": v(-18.76, -16.61) * mm, "end": v(-18.95, -17.55) * mm});
            skLineSegment(sketch, "E384", {"start": v(-18.95, -17.55) * mm, "end": v(-18.76, -18.48) * mm});
            skLineSegment(sketch, "E385", {"start": v(-18.76, -18.48) * mm, "end": v(-18.24, -19.24) * mm});
            skLineSegment(sketch, "E386", {"start": v(-18.24, -19.24) * mm, "end": v(-17.48, -19.76) * mm});
            skLineSegment(sketch, "E387", {"start": v(-17.48, -19.76) * mm, "end": v(-16.55, -19.95) * mm});
            skLineSegment(sketch, "E388", {"start": v(-16.55, -19.95) * mm, "end": v(-15.61, -19.76) * mm});
            skLineSegment(sketch, "E389", {"start": v(-15.61, -19.76) * mm, "end": v(-14.85, -19.24) * mm});
            skLineSegment(sketch, "E390", {"start": v(-14.85, -19.24) * mm, "end": v(-14.34, -18.48) * mm});
            skLineSegment(sketch, "E391", {"start": v(-14.34, -18.48) * mm, "end": v(-14.15, -17.55) * mm});
            skLineSegment(sketch, "E392", {"start": v(-5.9, -10.9) * mm, "end": v(-6.22, -9.34) * mm});
            skLineSegment(sketch, "E393", {"start": v(-6.22, -9.34) * mm, "end": v(-7.07, -8.07) * mm});
            skLineSegment(sketch, "E394", {"start": v(-7.07, -8.07) * mm, "end": v(-8.34, -7.21) * mm});
            skLineSegment(sketch, "E395", {"start": v(-8.34, -7.21) * mm, "end": v(-9.9, -6.9) * mm});
            skLineSegment(sketch, "E396", {"start": v(-9.9, -6.9) * mm, "end": v(-11.46, -7.21) * mm});
            skLineSegment(sketch, "E397", {"start": v(-11.46, -7.21) * mm, "end": v(-12.73, -8.07) * mm});
            skLineSegment(sketch, "E398", {"start": v(-12.73, -8.07) * mm, "end": v(-13.59, -9.34) * mm});
            skLineSegment(sketch, "E399", {"start": v(-13.59, -9.34) * mm, "end": v(-13.9, -10.9) * mm});
            skLineSegment(sketch, "E400", {"start": v(-13.9, -10.9) * mm, "end": v(-13.59, -12.46) * mm});
            skLineSegment(sketch, "E401", {"start": v(-13.59, -12.46) * mm, "end": v(-12.73, -13.73) * mm});
            skLineSegment(sketch, "E402", {"start": v(-12.73, -13.73) * mm, "end": v(-11.46, -14.58) * mm});
            skLineSegment(sketch, "E403", {"start": v(-11.46, -14.58) * mm, "end": v(-9.9, -14.9) * mm});
            skLineSegment(sketch, "E404", {"start": v(-9.9, -14.9) * mm, "end": v(-8.34, -14.58) * mm});
            skLineSegment(sketch, "E405", {"start": v(-8.34, -14.58) * mm, "end": v(-7.07, -13.73) * mm});
            skLineSegment(sketch, "E406", {"start": v(-7.07, -13.73) * mm, "end": v(-6.22, -12.46) * mm});
            skLineSegment(sketch, "E407", {"start": v(-6.22, -12.46) * mm, "end": v(-5.9, -10.9) * mm});
            skLineSegment(sketch, "E408", {"start": v(-4.9, -21.51) * mm, "end": v(-5.18, -20.1) * mm});
            skLineSegment(sketch, "E409", {"start": v(-5.18, -20.1) * mm, "end": v(-5.95, -18.96) * mm});
            skLineSegment(sketch, "E410", {"start": v(-5.95, -18.96) * mm, "end": v(-7.1, -18.2) * mm});
            skLineSegment(sketch, "E411", {"start": v(-7.1, -18.2) * mm, "end": v(-8.5, -17.9) * mm});
            skLineSegment(sketch, "E412", {"start": v(-8.5, -17.9) * mm, "end": v(-9.9, -18.2) * mm});
            skLineSegment(sketch, "E413", {"start": v(-9.9, -18.2) * mm, "end": v(-11.04, -18.96) * mm});
            skLineSegment(sketch, "E414", {"start": v(-11.04, -18.96) * mm, "end": v(-11.81, -20.1) * mm});
            skLineSegment(sketch, "E415", {"start": v(-11.81, -20.1) * mm, "end": v(-12.1, -21.51) * mm});
            skLineSegment(sketch, "E416", {"start": v(-12.1, -21.51) * mm, "end": v(-11.81, -22.91) * mm});
            skLineSegment(sketch, "E417", {"start": v(-11.81, -22.91) * mm, "end": v(-11.04, -24.05) * mm});
            skLineSegment(sketch, "E418", {"start": v(-11.04, -24.05) * mm, "end": v(-9.9, -24.83) * mm});
            skLineSegment(sketch, "E419", {"start": v(-9.9, -24.83) * mm, "end": v(-8.5, -25.1) * mm});
            skLineSegment(sketch, "E420", {"start": v(-8.5, -25.1) * mm, "end": v(-7.1, -24.83) * mm});
            skLineSegment(sketch, "E421", {"start": v(-7.1, -24.83) * mm, "end": v(-5.95, -24.05) * mm});
            skLineSegment(sketch, "E422", {"start": v(-5.95, -24.05) * mm, "end": v(-5.18, -22.91) * mm});
            skLineSegment(sketch, "E423", {"start": v(-5.18, -22.91) * mm, "end": v(-4.9, -21.51) * mm});
            skLineSegment(sketch, "E424", {"start": v(18.95, 15.55) * mm, "end": v(18.76, 16.48) * mm});
            skLineSegment(sketch, "E425", {"start": v(18.76, 16.48) * mm, "end": v(18.24, 17.24) * mm});
            skLineSegment(sketch, "E426", {"start": v(18.24, 17.24) * mm, "end": v(17.48, 17.76) * mm});
            skLineSegment(sketch, "E427", {"start": v(17.48, 17.76) * mm, "end": v(16.55, 17.95) * mm});
            skLineSegment(sketch, "E428", {"start": v(16.55, 17.95) * mm, "end": v(15.61, 17.76) * mm});
            skLineSegment(sketch, "E429", {"start": v(15.61, 17.76) * mm, "end": v(14.85, 17.24) * mm});
            skLineSegment(sketch, "E430", {"start": v(14.85, 17.24) * mm, "end": v(14.33, 16.48) * mm});
            skLineSegment(sketch, "E431", {"start": v(14.33, 16.48) * mm, "end": v(14.15, 15.55) * mm});
            skLineSegment(sketch, "E432", {"start": v(14.15, 15.55) * mm, "end": v(14.33, 14.61) * mm});
            skLineSegment(sketch, "E433", {"start": v(14.33, 14.61) * mm, "end": v(14.85, 13.85) * mm});
            skLineSegment(sketch, "E434", {"start": v(14.85, 13.85) * mm, "end": v(15.61, 13.34) * mm});
            skLineSegment(sketch, "E435", {"start": v(15.61, 13.34) * mm, "end": v(16.55, 13.15) * mm});
            skLineSegment(sketch, "E436", {"start": v(16.55, 13.15) * mm, "end": v(17.48, 13.34) * mm});
            skLineSegment(sketch, "E437", {"start": v(17.48, 13.34) * mm, "end": v(18.24, 13.85) * mm});
            skLineSegment(sketch, "E438", {"start": v(18.24, 13.85) * mm, "end": v(18.76, 14.61) * mm});
            skLineSegment(sketch, "E439", {"start": v(18.76, 14.61) * mm, "end": v(18.95, 15.55) * mm});
            skLineSegment(sketch, "E440", {"start": v(13.9, 8.9) * mm, "end": v(13.58, 10.46) * mm});
            skLineSegment(sketch, "E441", {"start": v(13.58, 10.46) * mm, "end": v(12.73, 11.73) * mm});
            skLineSegment(sketch, "E442", {"start": v(12.73, 11.73) * mm, "end": v(11.45, 12.58) * mm});
            skLineSegment(sketch, "E443", {"start": v(11.45, 12.58) * mm, "end": v(9.9, 12.9) * mm});
            skLineSegment(sketch, "E444", {"start": v(9.9, 12.9) * mm, "end": v(8.34, 12.58) * mm});
            skLineSegment(sketch, "E445", {"start": v(8.34, 12.58) * mm, "end": v(7.07, 11.73) * mm});
            skLineSegment(sketch, "E446", {"start": v(7.07, 11.73) * mm, "end": v(6.21, 10.46) * mm});
            skLineSegment(sketch, "E447", {"start": v(6.21, 10.46) * mm, "end": v(5.9, 8.9) * mm});
            skLineSegment(sketch, "E448", {"start": v(5.9, 8.9) * mm, "end": v(6.21, 7.34) * mm});
            skLineSegment(sketch, "E449", {"start": v(6.21, 7.34) * mm, "end": v(7.07, 6.07) * mm});
            skLineSegment(sketch, "E450", {"start": v(7.07, 6.07) * mm, "end": v(8.34, 5.21) * mm});
            skLineSegment(sketch, "E451", {"start": v(8.34, 5.21) * mm, "end": v(9.9, 4.9) * mm});
            skLineSegment(sketch, "E452", {"start": v(9.9, 4.9) * mm, "end": v(11.45, 5.21) * mm});
            skLineSegment(sketch, "E453", {"start": v(11.45, 5.21) * mm, "end": v(12.73, 6.07) * mm});
            skLineSegment(sketch, "E454", {"start": v(12.73, 6.07) * mm, "end": v(13.58, 7.34) * mm});
            skLineSegment(sketch, "E455", {"start": v(13.58, 7.34) * mm, "end": v(13.9, 8.9) * mm});
            skLineSegment(sketch, "E456", {"start": v(12.1, 19.5) * mm, "end": v(11.81, 20.91) * mm});
            skLineSegment(sketch, "E457", {"start": v(11.81, 20.91) * mm, "end": v(11.04, 22.06) * mm});
            skLineSegment(sketch, "E458", {"start": v(11.04, 22.06) * mm, "end": v(9.9, 22.83) * mm});
            skLineSegment(sketch, "E459", {"start": v(9.9, 22.83) * mm, "end": v(8.5, 23.11) * mm});
            skLineSegment(sketch, "E460", {"start": v(8.5, 23.11) * mm, "end": v(7.1, 22.83) * mm});
            skLineSegment(sketch, "E461", {"start": v(7.1, 22.83) * mm, "end": v(5.95, 22.06) * mm});
            skLineSegment(sketch, "E462", {"start": v(5.95, 22.06) * mm, "end": v(5.18, 20.91) * mm});
            skLineSegment(sketch, "E463", {"start": v(5.18, 20.91) * mm, "end": v(4.9, 19.5) * mm});
            skLineSegment(sketch, "E464", {"start": v(4.9, 19.5) * mm, "end": v(5.18, 18.1) * mm});
            skLineSegment(sketch, "E465", {"start": v(5.18, 18.1) * mm, "end": v(5.95, 16.97) * mm});
            skLineSegment(sketch, "E466", {"start": v(5.95, 16.97) * mm, "end": v(7.1, 16.2) * mm});
            skLineSegment(sketch, "E467", {"start": v(7.1, 16.2) * mm, "end": v(8.5, 15.91) * mm});
            skLineSegment(sketch, "E468", {"start": v(8.5, 15.91) * mm, "end": v(9.9, 16.2) * mm});
            skLineSegment(sketch, "E469", {"start": v(9.9, 16.2) * mm, "end": v(11.04, 16.97) * mm});
            skLineSegment(sketch, "E470", {"start": v(11.04, 16.97) * mm, "end": v(11.81, 18.1) * mm});
            skLineSegment(sketch, "E471", {"start": v(11.81, 18.1) * mm, "end": v(12.1, 19.5) * mm});
            skLineSegment(sketch, "E472", {"start": v(-32.18, -7.5) * mm, "end": v(-28.44, -37) * mm});
            skLineSegment(sketch, "E473", {"start": v(32.5, -2.48) * mm, "end": v(32.5, -1.28) * mm});
            skLineSegment(sketch, "E474", {"start": v(32.4, -0.2) * mm, "end": v(32.5, -1.28) * mm});
            skLineSegment(sketch, "E475", {"start": v(28.44, -37) * mm, "end": v(32.18, -7.5) * mm});
            skSolve(sketch);
        }
        {
            var Q0;
            Q0 = qSketchRegion(id + "F0", true);
            extrude(context, id + "F1", {"entities" : qUnion([Q0]), "depth" : 2 * mm});
        }
        {
            var Q0;
            Q0=makeQuery(id+"F1.opExtrude","CAP_FACE",FACE,{"disambiguationData":[OSD([sQuery(id+"F0.wireOp",EDGE,"E1"),sQuery(id+"F0.wireOp",EDGE,"E3"),sQuery(id+"F0.wireOp",EDGE,"E4"),sQuery(id+"F0.wireOp",EDGE,"E5"),sQuery(id+"F0.wireOp",EDGE,"E6"),sQuery(id+"F0.wireOp",EDGE,"E7"),sQuery(id+"F0.wireOp",EDGE,"E8"),sQuery(id+"F0.wireOp",EDGE,"E9"),sQuery(id+"F0.wireOp",EDGE,"E10"),sQuery(id+"F0.wireOp",EDGE,"E11"),sQuery(id+"F0.wireOp",EDGE,"E12"),sQuery(id+"F0.wireOp",EDGE,"E13"),sQuery(id+"F0.wireOp",EDGE,"E14"),sQuery(id+"F0.wireOp",EDGE,"E15"),sQuery(id+"F0.wireOp",EDGE,"E16"),sQuery(id+"F0.wireOp",EDGE,"E17"),sQuery(id+"F0.wireOp",EDGE,"E18"),sQuery(id+"F0.wireOp",EDGE,"E19"),sQuery(id+"F0.wireOp",EDGE,"E20"),sQuery(id+"F0.wireOp",EDGE,"E21"),sQuery(id+"F0.wireOp",EDGE,"E22"),sQuery(id+"F0.wireOp",EDGE,"E23"),sQuery(id+"F0.wireOp",EDGE,"E25"),sQuery(id+"F0.wireOp",EDGE,"E26"),sQuery(id+"F0.wireOp",EDGE,"E27"),sQuery(id+"F0.wireOp",EDGE,"E28"),sQuery(id+"F0.wireOp",EDGE,"E29"),sQuery(id+"F0.wireOp",EDGE,"E30"),sQuery(id+"F0.wireOp",EDGE,"E31"),sQuery(id+"F0.wireOp",EDGE,"E32"),sQuery(id+"F0.wireOp",EDGE,"E33"),sQuery(id+"F0.wireOp",EDGE,"E34"),sQuery(id+"F0.wireOp",EDGE,"E35"),sQuery(id+"F0.wireOp",EDGE,"E36"),sQuery(id+"F0.wireOp",EDGE,"E37"),sQuery(id+"F0.wireOp",EDGE,"E39"),sQuery(id+"F0.wireOp",EDGE,"E40"),sQuery(id+"F0.wireOp",EDGE,"E41"),sQuery(id+"F0.wireOp",EDGE,"E42"),sQuery(id+"F0.wireOp",EDGE,"E43"),sQuery(id+"F0.wireOp",EDGE,"E44"),sQuery(id+"F0.wireOp",EDGE,"E45"),sQuery(id+"F0.wireOp",EDGE,"E46"),sQuery(id+"F0.wireOp",EDGE,"E47"),sQuery(id+"F0.wireOp",EDGE,"E48"),sQuery(id+"F0.wireOp",EDGE,"E49"),sQuery(id+"F0.wireOp",EDGE,"E50"),sQuery(id+"F0.wireOp",EDGE,"E51"),sQuery(id+"F0.wireOp",EDGE,"E52"),sQuery(id+"F0.wireOp",EDGE,"E53"),sQuery(id+"F0.wireOp",EDGE,"E54"),sQuery(id+"F0.wireOp",EDGE,"E55"),sQuery(id+"F0.wireOp",EDGE,"E56"),sQuery(id+"F0.wireOp",EDGE,"E57"),sQuery(id+"F0.wireOp",EDGE,"E58"),sQuery(id+"F0.wireOp",EDGE,"E59"),sQuery(id+"F0.wireOp",EDGE,"E60"),sQuery(id+"F0.wireOp",EDGE,"E61"),sQuery(id+"F0.wireOp",EDGE,"E62"),sQuery(id+"F0.wireOp",EDGE,"E63"),sQuery(id+"F0.wireOp",EDGE,"E64"),sQuery(id+"F0.wireOp",EDGE,"E65"),sQuery(id+"F0.wireOp",EDGE,"E66"),sQuery(id+"F0.wireOp",EDGE,"E67"),sQuery(id+"F0.wireOp",EDGE,"E68"),sQuery(id+"F0.wireOp",EDGE,"E69"),sQuery(id+"F0.wireOp",EDGE,"E70"),sQuery(id+"F0.wireOp",EDGE,"E71"),sQuery(id+"F0.wireOp",EDGE,"E72"),sQuery(id+"F0.wireOp",EDGE,"E73"),sQuery(id+"F0.wireOp",EDGE,"E74"),sQuery(id+"F0.wireOp",EDGE,"E75"),sQuery(id+"F0.wireOp",EDGE,"E76"),sQuery(id+"F0.wireOp",EDGE,"E77"),sQuery(id+"F0.wireOp",EDGE,"E78"),sQuery(id+"F0.wireOp",EDGE,"E79"),sQuery(id+"F0.wireOp",EDGE,"E80"),sQuery(id+"F0.wireOp",EDGE,"E81"),sQuery(id+"F0.wireOp",EDGE,"E82"),sQuery(id+"F0.wireOp",EDGE,"E83"),sQuery(id+"F0.wireOp",EDGE,"E84"),sQuery(id+"F0.wireOp",EDGE,"E85"),sQuery(id+"F0.wireOp",EDGE,"E86"),sQuery(id+"F0.wireOp",EDGE,"E87"),sQuery(id+"F0.wireOp",EDGE,"E88"),sQuery(id+"F0.wireOp",EDGE,"E89"),sQuery(id+"F0.wireOp",EDGE,"E90"),sQuery(id+"F0.wireOp",EDGE,"E91"),sQuery(id+"F0.wireOp",EDGE,"E92"),sQuery(id+"F0.wireOp",EDGE,"E93"),sQuery(id+"F0.wireOp",EDGE,"E94"),sQuery(id+"F0.wireOp",EDGE,"E95"),sQuery(id+"F0.wireOp",EDGE,"E96"),sQuery(id+"F0.wireOp",EDGE,"E97"),sQuery(id+"F0.wireOp",EDGE,"E98"),sQuery(id+"F0.wireOp",EDGE,"E99"),sQuery(id+"F0.wireOp",EDGE,"E100"),sQuery(id+"F0.wireOp",EDGE,"E101"),sQuery(id+"F0.wireOp",EDGE,"E102"),sQuery(id+"F0.wireOp",EDGE,"E103"),sQuery(id+"F0.wireOp",EDGE,"E104"),sQuery(id+"F0.wireOp",EDGE,"E105"),sQuery(id+"F0.wireOp",EDGE,"E106"),sQuery(id+"F0.wireOp",EDGE,"E107"),sQuery(id+"F0.wireOp",EDGE,"E108"),sQuery(id+"F0.wireOp",EDGE,"E109"),sQuery(id+"F0.wireOp",EDGE,"E110"),sQuery(id+"F0.wireOp",EDGE,"E111"),sQuery(id+"F0.wireOp",EDGE,"E112"),sQuery(id+"F0.wireOp",EDGE,"E113"),sQuery(id+"F0.wireOp",EDGE,"E114"),sQuery(id+"F0.wireOp",EDGE,"E115"),sQuery(id+"F0.wireOp",EDGE,"E116"),sQuery(id+"F0.wireOp",EDGE,"E117"),sQuery(id+"F0.wireOp",EDGE,"E118"),sQuery(id+"F0.wireOp",EDGE,"E119"),sQuery(id+"F0.wireOp",EDGE,"E120"),sQuery(id+"F0.wireOp",EDGE,"E121"),sQuery(id+"F0.wireOp",EDGE,"E122"),sQuery(id+"F0.wireOp",EDGE,"E123"),sQuery(id+"F0.wireOp",EDGE,"E124"),sQuery(id+"F0.wireOp",EDGE,"E125"),sQuery(id+"F0.wireOp",EDGE,"E126"),sQuery(id+"F0.wireOp",EDGE,"E127"),sQuery(id+"F0.wireOp",EDGE,"E128"),sQuery(id+"F0.wireOp",EDGE,"E129"),sQuery(id+"F0.wireOp",EDGE,"E130"),sQuery(id+"F0.wireOp",EDGE,"E131"),sQuery(id+"F0.wireOp",EDGE,"E132"),sQuery(id+"F0.wireOp",EDGE,"E133"),sQuery(id+"F0.wireOp",EDGE,"E134"),sQuery(id+"F0.wireOp",EDGE,"E135"),sQuery(id+"F0.wireOp",EDGE,"E136"),sQuery(id+"F0.wireOp",EDGE,"E137"),sQuery(id+"F0.wireOp",EDGE,"E138"),sQuery(id+"F0.wireOp",EDGE,"E139"),sQuery(id+"F0.wireOp",EDGE,"E140"),sQuery(id+"F0.wireOp",EDGE,"E141"),sQuery(id+"F0.wireOp",EDGE,"E142"),sQuery(id+"F0.wireOp",EDGE,"E143"),sQuery(id+"F0.wireOp",EDGE,"E144"),sQuery(id+"F0.wireOp",EDGE,"E145"),sQuery(id+"F0.wireOp",EDGE,"E146"),sQuery(id+"F0.wireOp",EDGE,"E147"),sQuery(id+"F0.wireOp",EDGE,"E148"),sQuery(id+"F0.wireOp",EDGE,"E149"),sQuery(id+"F0.wireOp",EDGE,"E150"),sQuery(id+"F0.wireOp",EDGE,"E151"),sQuery(id+"F0.wireOp",EDGE,"E152"),sQuery(id+"F0.wireOp",EDGE,"E153"),sQuery(id+"F0.wireOp",EDGE,"E154"),sQuery(id+"F0.wireOp",EDGE,"E155"),sQuery(id+"F0.wireOp",EDGE,"E156"),sQuery(id+"F0.wireOp",EDGE,"E157"),sQuery(id+"F0.wireOp",EDGE,"E158"),sQuery(id+"F0.wireOp",EDGE,"E159"),sQuery(id+"F0.wireOp",EDGE,"E160"),sQuery(id+"F0.wireOp",EDGE,"E161"),sQuery(id+"F0.wireOp",EDGE,"E162"),sQuery(id+"F0.wireOp",EDGE,"E163"),sQuery(id+"F0.wireOp",EDGE,"E164"),sQuery(id+"F0.wireOp",EDGE,"E165"),sQuery(id+"F0.wireOp",EDGE,"E166"),sQuery(id+"F0.wireOp",EDGE,"E167"),sQuery(id+"F0.wireOp",EDGE,"E168"),sQuery(id+"F0.wireOp",EDGE,"E169"),sQuery(id+"F0.wireOp",EDGE,"E170"),sQuery(id+"F0.wireOp",EDGE,"E171"),sQuery(id+"F0.wireOp",EDGE,"E172"),sQuery(id+"F0.wireOp",EDGE,"E173"),sQuery(id+"F0.wireOp",EDGE,"E174"),sQuery(id+"F0.wireOp",EDGE,"E175"),sQuery(id+"F0.wireOp",EDGE,"E176"),sQuery(id+"F0.wireOp",EDGE,"E177"),sQuery(id+"F0.wireOp",EDGE,"E178"),sQuery(id+"F0.wireOp",EDGE,"E179"),sQuery(id+"F0.wireOp",EDGE,"E180"),sQuery(id+"F0.wireOp",EDGE,"E181"),sQuery(id+"F0.wireOp",EDGE,"E182"),sQuery(id+"F0.wireOp",EDGE,"E183"),sQuery(id+"F0.wireOp",EDGE,"E184"),sQuery(id+"F0.wireOp",EDGE,"E185"),sQuery(id+"F0.wireOp",EDGE,"E186"),sQuery(id+"F0.wireOp",EDGE,"E187"),sQuery(id+"F0.wireOp",EDGE,"E188"),sQuery(id+"F0.wireOp",EDGE,"E189"),sQuery(id+"F0.wireOp",EDGE,"E190"),sQuery(id+"F0.wireOp",EDGE,"E191"),sQuery(id+"F0.wireOp",EDGE,"E192"),sQuery(id+"F0.wireOp",EDGE,"E193"),sQuery(id+"F0.wireOp",EDGE,"E194"),sQuery(id+"F0.wireOp",EDGE,"E195"),sQuery(id+"F0.wireOp",EDGE,"E196"),sQuery(id+"F0.wireOp",EDGE,"E197"),sQuery(id+"F0.wireOp",EDGE,"E198"),sQuery(id+"F0.wireOp",EDGE,"E199"),sQuery(id+"F0.wireOp",EDGE,"E200"),sQuery(id+"F0.wireOp",EDGE,"E201"),sQuery(id+"F0.wireOp",EDGE,"E202"),sQuery(id+"F0.wireOp",EDGE,"E203"),sQuery(id+"F0.wireOp",EDGE,"E204"),sQuery(id+"F0.wireOp",EDGE,"E205"),sQuery(id+"F0.wireOp",EDGE,"E206"),sQuery(id+"F0.wireOp",EDGE,"E207"),sQuery(id+"F0.wireOp",EDGE,"E208"),sQuery(id+"F0.wireOp",EDGE,"E209"),sQuery(id+"F0.wireOp",EDGE,"E210"),sQuery(id+"F0.wireOp",EDGE,"E211"),sQuery(id+"F0.wireOp",EDGE,"E212"),sQuery(id+"F0.wireOp",EDGE,"E213"),sQuery(id+"F0.wireOp",EDGE,"E214"),sQuery(id+"F0.wireOp",EDGE,"E215"),sQuery(id+"F0.wireOp",EDGE,"E216"),sQuery(id+"F0.wireOp",EDGE,"E217"),sQuery(id+"F0.wireOp",EDGE,"E218"),sQuery(id+"F0.wireOp",EDGE,"E219"),sQuery(id+"F0.wireOp",EDGE,"E220"),sQuery(id+"F0.wireOp",EDGE,"E221"),sQuery(id+"F0.wireOp",EDGE,"E222"),sQuery(id+"F0.wireOp",EDGE,"E223"),sQuery(id+"F0.wireOp",EDGE,"E224"),sQuery(id+"F0.wireOp",EDGE,"E225"),sQuery(id+"F0.wireOp",EDGE,"E226"),sQuery(id+"F0.wireOp",EDGE,"E227"),sQuery(id+"F0.wireOp",EDGE,"E228"),sQuery(id+"F0.wireOp",EDGE,"E229"),sQuery(id+"F0.wireOp",EDGE,"E230"),sQuery(id+"F0.wireOp",EDGE,"E231"),sQuery(id+"F0.wireOp",EDGE,"E232"),sQuery(id+"F0.wireOp",EDGE,"E233"),sQuery(id+"F0.wireOp",EDGE,"E234"),sQuery(id+"F0.wireOp",EDGE,"E235"),sQuery(id+"F0.wireOp",EDGE,"E236"),sQuery(id+"F0.wireOp",EDGE,"E237"),sQuery(id+"F0.wireOp",EDGE,"E238"),sQuery(id+"F0.wireOp",EDGE,"E239"),sQuery(id+"F0.wireOp",EDGE,"E240"),sQuery(id+"F0.wireOp",EDGE,"E241"),sQuery(id+"F0.wireOp",EDGE,"E242"),sQuery(id+"F0.wireOp",EDGE,"E243"),sQuery(id+"F0.wireOp",EDGE,"E244"),sQuery(id+"F0.wireOp",EDGE,"E245"),sQuery(id+"F0.wireOp",EDGE,"E246"),sQuery(id+"F0.wireOp",EDGE,"E247"),sQuery(id+"F0.wireOp",EDGE,"E248"),sQuery(id+"F0.wireOp",EDGE,"E249"),sQuery(id+"F0.wireOp",EDGE,"E250"),sQuery(id+"F0.wireOp",EDGE,"E251"),sQuery(id+"F0.wireOp",EDGE,"E252"),sQuery(id+"F0.wireOp",EDGE,"E253"),sQuery(id+"F0.wireOp",EDGE,"E254"),sQuery(id+"F0.wireOp",EDGE,"E255"),sQuery(id+"F0.wireOp",EDGE,"E256"),sQuery(id+"F0.wireOp",EDGE,"E257"),sQuery(id+"F0.wireOp",EDGE,"E258"),sQuery(id+"F0.wireOp",EDGE,"E259"),sQuery(id+"F0.wireOp",EDGE,"E260"),sQuery(id+"F0.wireOp",EDGE,"E261"),sQuery(id+"F0.wireOp",EDGE,"E262"),sQuery(id+"F0.wireOp",EDGE,"E263"),sQuery(id+"F0.wireOp",EDGE,"E264"),sQuery(id+"F0.wireOp",EDGE,"E265"),sQuery(id+"F0.wireOp",EDGE,"E266"),sQuery(id+"F0.wireOp",EDGE,"E267"),sQuery(id+"F0.wireOp",EDGE,"E268"),sQuery(id+"F0.wireOp",EDGE,"E269"),sQuery(id+"F0.wireOp",EDGE,"E270"),sQuery(id+"F0.wireOp",EDGE,"E271"),sQuery(id+"F0.wireOp",EDGE,"E272"),sQuery(id+"F0.wireOp",EDGE,"E273"),sQuery(id+"F0.wireOp",EDGE,"E274"),sQuery(id+"F0.wireOp",EDGE,"E275"),sQuery(id+"F0.wireOp",EDGE,"E276"),sQuery(id+"F0.wireOp",EDGE,"E277"),sQuery(id+"F0.wireOp",EDGE,"E278"),sQuery(id+"F0.wireOp",EDGE,"E279"),sQuery(id+"F0.wireOp",EDGE,"E280"),sQuery(id+"F0.wireOp",EDGE,"E281"),sQuery(id+"F0.wireOp",EDGE,"E282"),sQuery(id+"F0.wireOp",EDGE,"E283"),sQuery(id+"F0.wireOp",EDGE,"E284"),sQuery(id+"F0.wireOp",EDGE,"E285"),sQuery(id+"F0.wireOp",EDGE,"E286"),sQuery(id+"F0.wireOp",EDGE,"E287"),sQuery(id+"F0.wireOp",EDGE,"E288"),sQuery(id+"F0.wireOp",EDGE,"E289"),sQuery(id+"F0.wireOp",EDGE,"E290"),sQuery(id+"F0.wireOp",EDGE,"E291"),sQuery(id+"F0.wireOp",EDGE,"E292"),sQuery(id+"F0.wireOp",EDGE,"E293"),sQuery(id+"F0.wireOp",EDGE,"E294"),sQuery(id+"F0.wireOp",EDGE,"E295"),sQuery(id+"F0.wireOp",EDGE,"E296"),sQuery(id+"F0.wireOp",EDGE,"E297"),sQuery(id+"F0.wireOp",EDGE,"E298"),sQuery(id+"F0.wireOp",EDGE,"E299"),sQuery(id+"F0.wireOp",EDGE,"E300"),sQuery(id+"F0.wireOp",EDGE,"E301"),sQuery(id+"F0.wireOp",EDGE,"E302"),sQuery(id+"F0.wireOp",EDGE,"E303"),sQuery(id+"F0.wireOp",EDGE,"E304"),sQuery(id+"F0.wireOp",EDGE,"E305"),sQuery(id+"F0.wireOp",EDGE,"E306"),sQuery(id+"F0.wireOp",EDGE,"E307"),sQuery(id+"F0.wireOp",EDGE,"E308"),sQuery(id+"F0.wireOp",EDGE,"E309"),sQuery(id+"F0.wireOp",EDGE,"E310"),sQuery(id+"F0.wireOp",EDGE,"E311"),sQuery(id+"F0.wireOp",EDGE,"E312"),sQuery(id+"F0.wireOp",EDGE,"E313"),sQuery(id+"F0.wireOp",EDGE,"E314"),sQuery(id+"F0.wireOp",EDGE,"E315"),sQuery(id+"F0.wireOp",EDGE,"E316"),sQuery(id+"F0.wireOp",EDGE,"E317"),sQuery(id+"F0.wireOp",EDGE,"E318"),sQuery(id+"F0.wireOp",EDGE,"E319"),sQuery(id+"F0.wireOp",EDGE,"E320"),sQuery(id+"F0.wireOp",EDGE,"E321"),sQuery(id+"F0.wireOp",EDGE,"E322"),sQuery(id+"F0.wireOp",EDGE,"E323"),sQuery(id+"F0.wireOp",EDGE,"E324"),sQuery(id+"F0.wireOp",EDGE,"E325"),sQuery(id+"F0.wireOp",EDGE,"E326"),sQuery(id+"F0.wireOp",EDGE,"E327"),sQuery(id+"F0.wireOp",EDGE,"E328"),sQuery(id+"F0.wireOp",EDGE,"E329"),sQuery(id+"F0.wireOp",EDGE,"E330"),sQuery(id+"F0.wireOp",EDGE,"E331"),sQuery(id+"F0.wireOp",EDGE,"E332"),sQuery(id+"F0.wireOp",EDGE,"E333"),sQuery(id+"F0.wireOp",EDGE,"E334"),sQuery(id+"F0.wireOp",EDGE,"E335"),sQuery(id+"F0.wireOp",EDGE,"E336"),sQuery(id+"F0.wireOp",EDGE,"E337"),sQuery(id+"F0.wireOp",EDGE,"E338"),sQuery(id+"F0.wireOp",EDGE,"E339"),sQuery(id+"F0.wireOp",EDGE,"E340"),sQuery(id+"F0.wireOp",EDGE,"E341"),sQuery(id+"F0.wireOp",EDGE,"E342"),sQuery(id+"F0.wireOp",EDGE,"E343"),sQuery(id+"F0.wireOp",EDGE,"E344"),sQuery(id+"F0.wireOp",EDGE,"E345"),sQuery(id+"F0.wireOp",EDGE,"E346"),sQuery(id+"F0.wireOp",EDGE,"E347"),sQuery(id+"F0.wireOp",EDGE,"E348"),sQuery(id+"F0.wireOp",EDGE,"E349"),sQuery(id+"F0.wireOp",EDGE,"E350"),sQuery(id+"F0.wireOp",EDGE,"E351"),sQuery(id+"F0.wireOp",EDGE,"E352"),sQuery(id+"F0.wireOp",EDGE,"E353"),sQuery(id+"F0.wireOp",EDGE,"E354"),sQuery(id+"F0.wireOp",EDGE,"E355"),sQuery(id+"F0.wireOp",EDGE,"E356"),sQuery(id+"F0.wireOp",EDGE,"E357"),sQuery(id+"F0.wireOp",EDGE,"E358"),sQuery(id+"F0.wireOp",EDGE,"E359"),sQuery(id+"F0.wireOp",EDGE,"E360"),sQuery(id+"F0.wireOp",EDGE,"E361"),sQuery(id+"F0.wireOp",EDGE,"E362"),sQuery(id+"F0.wireOp",EDGE,"E363"),sQuery(id+"F0.wireOp",EDGE,"E364"),sQuery(id+"F0.wireOp",EDGE,"E365"),sQuery(id+"F0.wireOp",EDGE,"E366"),sQuery(id+"F0.wireOp",EDGE,"E367"),sQuery(id+"F0.wireOp",EDGE,"E368"),sQuery(id+"F0.wireOp",EDGE,"E369"),sQuery(id+"F0.wireOp",EDGE,"E370"),sQuery(id+"F0.wireOp",EDGE,"E371"),sQuery(id+"F0.wireOp",EDGE,"E372"),sQuery(id+"F0.wireOp",EDGE,"E373"),sQuery(id+"F0.wireOp",EDGE,"E374"),sQuery(id+"F0.wireOp",EDGE,"E375"),sQuery(id+"F0.wireOp",EDGE,"E376"),sQuery(id+"F0.wireOp",EDGE,"E377"),sQuery(id+"F0.wireOp",EDGE,"E378"),sQuery(id+"F0.wireOp",EDGE,"E379"),sQuery(id+"F0.wireOp",EDGE,"E380"),sQuery(id+"F0.wireOp",EDGE,"E381"),sQuery(id+"F0.wireOp",EDGE,"E382"),sQuery(id+"F0.wireOp",EDGE,"E383"),sQuery(id+"F0.wireOp",EDGE,"E384"),sQuery(id+"F0.wireOp",EDGE,"E385"),sQuery(id+"F0.wireOp",EDGE,"E386"),sQuery(id+"F0.wireOp",EDGE,"E387"),sQuery(id+"F0.wireOp",EDGE,"E388"),sQuery(id+"F0.wireOp",EDGE,"E389"),sQuery(id+"F0.wireOp",EDGE,"E390"),sQuery(id+"F0.wireOp",EDGE,"E391"),sQuery(id+"F0.wireOp",EDGE,"E392"),sQuery(id+"F0.wireOp",EDGE,"E393"),sQuery(id+"F0.wireOp",EDGE,"E394"),sQuery(id+"F0.wireOp",EDGE,"E395"),sQuery(id+"F0.wireOp",EDGE,"E396"),sQuery(id+"F0.wireOp",EDGE,"E397"),sQuery(id+"F0.wireOp",EDGE,"E398"),sQuery(id+"F0.wireOp",EDGE,"E399"),sQuery(id+"F0.wireOp",EDGE,"E400"),sQuery(id+"F0.wireOp",EDGE,"E401"),sQuery(id+"F0.wireOp",EDGE,"E402"),sQuery(id+"F0.wireOp",EDGE,"E403"),sQuery(id+"F0.wireOp",EDGE,"E404"),sQuery(id+"F0.wireOp",EDGE,"E405"),sQuery(id+"F0.wireOp",EDGE,"E406"),sQuery(id+"F0.wireOp",EDGE,"E407"),sQuery(id+"F0.wireOp",EDGE,"E408"),sQuery(id+"F0.wireOp",EDGE,"E409"),sQuery(id+"F0.wireOp",EDGE,"E410"),sQuery(id+"F0.wireOp",EDGE,"E411"),sQuery(id+"F0.wireOp",EDGE,"E412"),sQuery(id+"F0.wireOp",EDGE,"E413"),sQuery(id+"F0.wireOp",EDGE,"E414"),sQuery(id+"F0.wireOp",EDGE,"E415"),sQuery(id+"F0.wireOp",EDGE,"E416"),sQuery(id+"F0.wireOp",EDGE,"E417"),sQuery(id+"F0.wireOp",EDGE,"E418"),sQuery(id+"F0.wireOp",EDGE,"E419"),sQuery(id+"F0.wireOp",EDGE,"E420"),sQuery(id+"F0.wireOp",EDGE,"E421"),sQuery(id+"F0.wireOp",EDGE,"E422"),sQuery(id+"F0.wireOp",EDGE,"E423"),sQuery(id+"F0.wireOp",EDGE,"E424"),sQuery(id+"F0.wireOp",EDGE,"E425"),sQuery(id+"F0.wireOp",EDGE,"E426"),sQuery(id+"F0.wireOp",EDGE,"E427"),sQuery(id+"F0.wireOp",EDGE,"E428"),sQuery(id+"F0.wireOp",EDGE,"E429"),sQuery(id+"F0.wireOp",EDGE,"E430"),sQuery(id+"F0.wireOp",EDGE,"E431"),sQuery(id+"F0.wireOp",EDGE,"E432"),sQuery(id+"F0.wireOp",EDGE,"E433"),sQuery(id+"F0.wireOp",EDGE,"E434"),sQuery(id+"F0.wireOp",EDGE,"E435"),sQuery(id+"F0.wireOp",EDGE,"E436"),sQuery(id+"F0.wireOp",EDGE,"E437"),sQuery(id+"F0.wireOp",EDGE,"E438"),sQuery(id+"F0.wireOp",EDGE,"E439"),sQuery(id+"F0.wireOp",EDGE,"E440"),sQuery(id+"F0.wireOp",EDGE,"E441"),sQuery(id+"F0.wireOp",EDGE,"E442"),sQuery(id+"F0.wireOp",EDGE,"E443"),sQuery(id+"F0.wireOp",EDGE,"E444"),sQuery(id+"F0.wireOp",EDGE,"E445"),sQuery(id+"F0.wireOp",EDGE,"E446"),sQuery(id+"F0.wireOp",EDGE,"E447"),sQuery(id+"F0.wireOp",EDGE,"E448"),sQuery(id+"F0.wireOp",EDGE,"E449"),sQuery(id+"F0.wireOp",EDGE,"E450"),sQuery(id+"F0.wireOp",EDGE,"E451"),sQuery(id+"F0.wireOp",EDGE,"E452"),sQuery(id+"F0.wireOp",EDGE,"E453"),sQuery(id+"F0.wireOp",EDGE,"E454"),sQuery(id+"F0.wireOp",EDGE,"E455"),sQuery(id+"F0.wireOp",EDGE,"E456"),sQuery(id+"F0.wireOp",EDGE,"E457"),sQuery(id+"F0.wireOp",EDGE,"E458"),sQuery(id+"F0.wireOp",EDGE,"E459"),sQuery(id+"F0.wireOp",EDGE,"E460"),sQuery(id+"F0.wireOp",EDGE,"E461"),sQuery(id+"F0.wireOp",EDGE,"E462"),sQuery(id+"F0.wireOp",EDGE,"E463"),sQuery(id+"F0.wireOp",EDGE,"E464"),sQuery(id+"F0.wireOp",EDGE,"E465"),sQuery(id+"F0.wireOp",EDGE,"E466"),sQuery(id+"F0.wireOp",EDGE,"E467"),sQuery(id+"F0.wireOp",EDGE,"E468"),sQuery(id+"F0.wireOp",EDGE,"E469"),sQuery(id+"F0.wireOp",EDGE,"E470"),sQuery(id+"F0.wireOp",EDGE,"E471"),sQuery(id+"F0.wireOp",EDGE,"E472"),sQuery(id+"F0.wireOp",EDGE,"E473"),sQuery(id+"F0.wireOp",EDGE,"E474"),sQuery(id+"F0.wireOp",EDGE,"E475")])],"isStart":false});
            fillet(context, id + "F2", {"entities" : qUnion([Q0]), "radius" : 1 * mm, "tangentPropagation" : true, "allowEdgeOverflow" : false});
        }
        {
            var Q0;
            Q0=makeQuery(id+"F1.opExtrude","CAP_FACE",FACE,{"disambiguationData":[OSD([sQuery(id+"F0.wireOp",EDGE,"E1"),sQuery(id+"F0.wireOp",EDGE,"E3"),sQuery(id+"F0.wireOp",EDGE,"E4"),sQuery(id+"F0.wireOp",EDGE,"E5"),sQuery(id+"F0.wireOp",EDGE,"E6"),sQuery(id+"F0.wireOp",EDGE,"E7"),sQuery(id+"F0.wireOp",EDGE,"E8"),sQuery(id+"F0.wireOp",EDGE,"E9"),sQuery(id+"F0.wireOp",EDGE,"E10"),sQuery(id+"F0.wireOp",EDGE,"E11"),sQuery(id+"F0.wireOp",EDGE,"E12"),sQuery(id+"F0.wireOp",EDGE,"E13"),sQuery(id+"F0.wireOp",EDGE,"E14"),sQuery(id+"F0.wireOp",EDGE,"E15"),sQuery(id+"F0.wireOp",EDGE,"E16"),sQuery(id+"F0.wireOp",EDGE,"E17"),sQuery(id+"F0.wireOp",EDGE,"E18"),sQuery(id+"F0.wireOp",EDGE,"E19"),sQuery(id+"F0.wireOp",EDGE,"E20"),sQuery(id+"F0.wireOp",EDGE,"E21"),sQuery(id+"F0.wireOp",EDGE,"E22"),sQuery(id+"F0.wireOp",EDGE,"E23"),sQuery(id+"F0.wireOp",EDGE,"E25"),sQuery(id+"F0.wireOp",EDGE,"E26"),sQuery(id+"F0.wireOp",EDGE,"E27"),sQuery(id+"F0.wireOp",EDGE,"E28"),sQuery(id+"F0.wireOp",EDGE,"E29"),sQuery(id+"F0.wireOp",EDGE,"E30"),sQuery(id+"F0.wireOp",EDGE,"E31"),sQuery(id+"F0.wireOp",EDGE,"E32"),sQuery(id+"F0.wireOp",EDGE,"E33"),sQuery(id+"F0.wireOp",EDGE,"E34"),sQuery(id+"F0.wireOp",EDGE,"E35"),sQuery(id+"F0.wireOp",EDGE,"E36"),sQuery(id+"F0.wireOp",EDGE,"E37"),sQuery(id+"F0.wireOp",EDGE,"E39"),sQuery(id+"F0.wireOp",EDGE,"E40"),sQuery(id+"F0.wireOp",EDGE,"E41"),sQuery(id+"F0.wireOp",EDGE,"E42"),sQuery(id+"F0.wireOp",EDGE,"E43"),sQuery(id+"F0.wireOp",EDGE,"E44"),sQuery(id+"F0.wireOp",EDGE,"E45"),sQuery(id+"F0.wireOp",EDGE,"E46"),sQuery(id+"F0.wireOp",EDGE,"E47"),sQuery(id+"F0.wireOp",EDGE,"E48"),sQuery(id+"F0.wireOp",EDGE,"E49"),sQuery(id+"F0.wireOp",EDGE,"E50"),sQuery(id+"F0.wireOp",EDGE,"E51"),sQuery(id+"F0.wireOp",EDGE,"E52"),sQuery(id+"F0.wireOp",EDGE,"E53"),sQuery(id+"F0.wireOp",EDGE,"E54"),sQuery(id+"F0.wireOp",EDGE,"E55"),sQuery(id+"F0.wireOp",EDGE,"E56"),sQuery(id+"F0.wireOp",EDGE,"E57"),sQuery(id+"F0.wireOp",EDGE,"E58"),sQuery(id+"F0.wireOp",EDGE,"E59"),sQuery(id+"F0.wireOp",EDGE,"E60"),sQuery(id+"F0.wireOp",EDGE,"E61"),sQuery(id+"F0.wireOp",EDGE,"E62"),sQuery(id+"F0.wireOp",EDGE,"E63"),sQuery(id+"F0.wireOp",EDGE,"E64"),sQuery(id+"F0.wireOp",EDGE,"E65"),sQuery(id+"F0.wireOp",EDGE,"E66"),sQuery(id+"F0.wireOp",EDGE,"E67"),sQuery(id+"F0.wireOp",EDGE,"E68"),sQuery(id+"F0.wireOp",EDGE,"E69"),sQuery(id+"F0.wireOp",EDGE,"E70"),sQuery(id+"F0.wireOp",EDGE,"E71"),sQuery(id+"F0.wireOp",EDGE,"E72"),sQuery(id+"F0.wireOp",EDGE,"E73"),sQuery(id+"F0.wireOp",EDGE,"E74"),sQuery(id+"F0.wireOp",EDGE,"E75"),sQuery(id+"F0.wireOp",EDGE,"E76"),sQuery(id+"F0.wireOp",EDGE,"E77"),sQuery(id+"F0.wireOp",EDGE,"E78"),sQuery(id+"F0.wireOp",EDGE,"E79"),sQuery(id+"F0.wireOp",EDGE,"E80"),sQuery(id+"F0.wireOp",EDGE,"E81"),sQuery(id+"F0.wireOp",EDGE,"E82"),sQuery(id+"F0.wireOp",EDGE,"E83"),sQuery(id+"F0.wireOp",EDGE,"E84"),sQuery(id+"F0.wireOp",EDGE,"E85"),sQuery(id+"F0.wireOp",EDGE,"E86"),sQuery(id+"F0.wireOp",EDGE,"E87"),sQuery(id+"F0.wireOp",EDGE,"E88"),sQuery(id+"F0.wireOp",EDGE,"E89"),sQuery(id+"F0.wireOp",EDGE,"E90"),sQuery(id+"F0.wireOp",EDGE,"E91"),sQuery(id+"F0.wireOp",EDGE,"E92"),sQuery(id+"F0.wireOp",EDGE,"E93"),sQuery(id+"F0.wireOp",EDGE,"E94"),sQuery(id+"F0.wireOp",EDGE,"E95"),sQuery(id+"F0.wireOp",EDGE,"E96"),sQuery(id+"F0.wireOp",EDGE,"E97"),sQuery(id+"F0.wireOp",EDGE,"E98"),sQuery(id+"F0.wireOp",EDGE,"E99"),sQuery(id+"F0.wireOp",EDGE,"E100"),sQuery(id+"F0.wireOp",EDGE,"E101"),sQuery(id+"F0.wireOp",EDGE,"E102"),sQuery(id+"F0.wireOp",EDGE,"E103"),sQuery(id+"F0.wireOp",EDGE,"E104"),sQuery(id+"F0.wireOp",EDGE,"E105"),sQuery(id+"F0.wireOp",EDGE,"E106"),sQuery(id+"F0.wireOp",EDGE,"E107"),sQuery(id+"F0.wireOp",EDGE,"E108"),sQuery(id+"F0.wireOp",EDGE,"E109"),sQuery(id+"F0.wireOp",EDGE,"E110"),sQuery(id+"F0.wireOp",EDGE,"E111"),sQuery(id+"F0.wireOp",EDGE,"E112"),sQuery(id+"F0.wireOp",EDGE,"E113"),sQuery(id+"F0.wireOp",EDGE,"E114"),sQuery(id+"F0.wireOp",EDGE,"E115"),sQuery(id+"F0.wireOp",EDGE,"E116"),sQuery(id+"F0.wireOp",EDGE,"E117"),sQuery(id+"F0.wireOp",EDGE,"E118"),sQuery(id+"F0.wireOp",EDGE,"E119"),sQuery(id+"F0.wireOp",EDGE,"E120"),sQuery(id+"F0.wireOp",EDGE,"E121"),sQuery(id+"F0.wireOp",EDGE,"E122"),sQuery(id+"F0.wireOp",EDGE,"E123"),sQuery(id+"F0.wireOp",EDGE,"E124"),sQuery(id+"F0.wireOp",EDGE,"E125"),sQuery(id+"F0.wireOp",EDGE,"E126"),sQuery(id+"F0.wireOp",EDGE,"E127"),sQuery(id+"F0.wireOp",EDGE,"E128"),sQuery(id+"F0.wireOp",EDGE,"E129"),sQuery(id+"F0.wireOp",EDGE,"E130"),sQuery(id+"F0.wireOp",EDGE,"E131"),sQuery(id+"F0.wireOp",EDGE,"E132"),sQuery(id+"F0.wireOp",EDGE,"E133"),sQuery(id+"F0.wireOp",EDGE,"E134"),sQuery(id+"F0.wireOp",EDGE,"E135"),sQuery(id+"F0.wireOp",EDGE,"E136"),sQuery(id+"F0.wireOp",EDGE,"E137"),sQuery(id+"F0.wireOp",EDGE,"E138"),sQuery(id+"F0.wireOp",EDGE,"E139"),sQuery(id+"F0.wireOp",EDGE,"E140"),sQuery(id+"F0.wireOp",EDGE,"E141"),sQuery(id+"F0.wireOp",EDGE,"E142"),sQuery(id+"F0.wireOp",EDGE,"E143"),sQuery(id+"F0.wireOp",EDGE,"E144"),sQuery(id+"F0.wireOp",EDGE,"E145"),sQuery(id+"F0.wireOp",EDGE,"E146"),sQuery(id+"F0.wireOp",EDGE,"E147"),sQuery(id+"F0.wireOp",EDGE,"E148"),sQuery(id+"F0.wireOp",EDGE,"E149"),sQuery(id+"F0.wireOp",EDGE,"E150"),sQuery(id+"F0.wireOp",EDGE,"E151"),sQuery(id+"F0.wireOp",EDGE,"E152"),sQuery(id+"F0.wireOp",EDGE,"E153"),sQuery(id+"F0.wireOp",EDGE,"E154"),sQuery(id+"F0.wireOp",EDGE,"E155"),sQuery(id+"F0.wireOp",EDGE,"E156"),sQuery(id+"F0.wireOp",EDGE,"E157"),sQuery(id+"F0.wireOp",EDGE,"E158"),sQuery(id+"F0.wireOp",EDGE,"E159"),sQuery(id+"F0.wireOp",EDGE,"E160"),sQuery(id+"F0.wireOp",EDGE,"E161"),sQuery(id+"F0.wireOp",EDGE,"E162"),sQuery(id+"F0.wireOp",EDGE,"E163"),sQuery(id+"F0.wireOp",EDGE,"E164"),sQuery(id+"F0.wireOp",EDGE,"E165"),sQuery(id+"F0.wireOp",EDGE,"E166"),sQuery(id+"F0.wireOp",EDGE,"E167"),sQuery(id+"F0.wireOp",EDGE,"E168"),sQuery(id+"F0.wireOp",EDGE,"E169"),sQuery(id+"F0.wireOp",EDGE,"E170"),sQuery(id+"F0.wireOp",EDGE,"E171"),sQuery(id+"F0.wireOp",EDGE,"E172"),sQuery(id+"F0.wireOp",EDGE,"E173"),sQuery(id+"F0.wireOp",EDGE,"E174"),sQuery(id+"F0.wireOp",EDGE,"E175"),sQuery(id+"F0.wireOp",EDGE,"E176"),sQuery(id+"F0.wireOp",EDGE,"E177"),sQuery(id+"F0.wireOp",EDGE,"E178"),sQuery(id+"F0.wireOp",EDGE,"E179"),sQuery(id+"F0.wireOp",EDGE,"E180"),sQuery(id+"F0.wireOp",EDGE,"E181"),sQuery(id+"F0.wireOp",EDGE,"E182"),sQuery(id+"F0.wireOp",EDGE,"E183"),sQuery(id+"F0.wireOp",EDGE,"E184"),sQuery(id+"F0.wireOp",EDGE,"E185"),sQuery(id+"F0.wireOp",EDGE,"E186"),sQuery(id+"F0.wireOp",EDGE,"E187"),sQuery(id+"F0.wireOp",EDGE,"E188"),sQuery(id+"F0.wireOp",EDGE,"E189"),sQuery(id+"F0.wireOp",EDGE,"E190"),sQuery(id+"F0.wireOp",EDGE,"E191"),sQuery(id+"F0.wireOp",EDGE,"E192"),sQuery(id+"F0.wireOp",EDGE,"E193"),sQuery(id+"F0.wireOp",EDGE,"E194"),sQuery(id+"F0.wireOp",EDGE,"E195"),sQuery(id+"F0.wireOp",EDGE,"E196"),sQuery(id+"F0.wireOp",EDGE,"E197"),sQuery(id+"F0.wireOp",EDGE,"E198"),sQuery(id+"F0.wireOp",EDGE,"E199"),sQuery(id+"F0.wireOp",EDGE,"E200"),sQuery(id+"F0.wireOp",EDGE,"E201"),sQuery(id+"F0.wireOp",EDGE,"E202"),sQuery(id+"F0.wireOp",EDGE,"E203"),sQuery(id+"F0.wireOp",EDGE,"E204"),sQuery(id+"F0.wireOp",EDGE,"E205"),sQuery(id+"F0.wireOp",EDGE,"E206"),sQuery(id+"F0.wireOp",EDGE,"E207"),sQuery(id+"F0.wireOp",EDGE,"E208"),sQuery(id+"F0.wireOp",EDGE,"E209"),sQuery(id+"F0.wireOp",EDGE,"E210"),sQuery(id+"F0.wireOp",EDGE,"E211"),sQuery(id+"F0.wireOp",EDGE,"E212"),sQuery(id+"F0.wireOp",EDGE,"E213"),sQuery(id+"F0.wireOp",EDGE,"E214"),sQuery(id+"F0.wireOp",EDGE,"E215"),sQuery(id+"F0.wireOp",EDGE,"E216"),sQuery(id+"F0.wireOp",EDGE,"E217"),sQuery(id+"F0.wireOp",EDGE,"E218"),sQuery(id+"F0.wireOp",EDGE,"E219"),sQuery(id+"F0.wireOp",EDGE,"E220"),sQuery(id+"F0.wireOp",EDGE,"E221"),sQuery(id+"F0.wireOp",EDGE,"E222"),sQuery(id+"F0.wireOp",EDGE,"E223"),sQuery(id+"F0.wireOp",EDGE,"E224"),sQuery(id+"F0.wireOp",EDGE,"E225"),sQuery(id+"F0.wireOp",EDGE,"E226"),sQuery(id+"F0.wireOp",EDGE,"E227"),sQuery(id+"F0.wireOp",EDGE,"E228"),sQuery(id+"F0.wireOp",EDGE,"E229"),sQuery(id+"F0.wireOp",EDGE,"E230"),sQuery(id+"F0.wireOp",EDGE,"E231"),sQuery(id+"F0.wireOp",EDGE,"E232"),sQuery(id+"F0.wireOp",EDGE,"E233"),sQuery(id+"F0.wireOp",EDGE,"E234"),sQuery(id+"F0.wireOp",EDGE,"E235"),sQuery(id+"F0.wireOp",EDGE,"E236"),sQuery(id+"F0.wireOp",EDGE,"E237"),sQuery(id+"F0.wireOp",EDGE,"E238"),sQuery(id+"F0.wireOp",EDGE,"E239"),sQuery(id+"F0.wireOp",EDGE,"E240"),sQuery(id+"F0.wireOp",EDGE,"E241"),sQuery(id+"F0.wireOp",EDGE,"E242"),sQuery(id+"F0.wireOp",EDGE,"E243"),sQuery(id+"F0.wireOp",EDGE,"E244"),sQuery(id+"F0.wireOp",EDGE,"E245"),sQuery(id+"F0.wireOp",EDGE,"E246"),sQuery(id+"F0.wireOp",EDGE,"E247"),sQuery(id+"F0.wireOp",EDGE,"E248"),sQuery(id+"F0.wireOp",EDGE,"E249"),sQuery(id+"F0.wireOp",EDGE,"E250"),sQuery(id+"F0.wireOp",EDGE,"E251"),sQuery(id+"F0.wireOp",EDGE,"E252"),sQuery(id+"F0.wireOp",EDGE,"E253"),sQuery(id+"F0.wireOp",EDGE,"E254"),sQuery(id+"F0.wireOp",EDGE,"E255"),sQuery(id+"F0.wireOp",EDGE,"E256"),sQuery(id+"F0.wireOp",EDGE,"E257"),sQuery(id+"F0.wireOp",EDGE,"E258"),sQuery(id+"F0.wireOp",EDGE,"E259"),sQuery(id+"F0.wireOp",EDGE,"E260"),sQuery(id+"F0.wireOp",EDGE,"E261"),sQuery(id+"F0.wireOp",EDGE,"E262"),sQuery(id+"F0.wireOp",EDGE,"E263"),sQuery(id+"F0.wireOp",EDGE,"E264"),sQuery(id+"F0.wireOp",EDGE,"E265"),sQuery(id+"F0.wireOp",EDGE,"E266"),sQuery(id+"F0.wireOp",EDGE,"E267"),sQuery(id+"F0.wireOp",EDGE,"E268"),sQuery(id+"F0.wireOp",EDGE,"E269"),sQuery(id+"F0.wireOp",EDGE,"E270"),sQuery(id+"F0.wireOp",EDGE,"E271"),sQuery(id+"F0.wireOp",EDGE,"E272"),sQuery(id+"F0.wireOp",EDGE,"E273"),sQuery(id+"F0.wireOp",EDGE,"E274"),sQuery(id+"F0.wireOp",EDGE,"E275"),sQuery(id+"F0.wireOp",EDGE,"E276"),sQuery(id+"F0.wireOp",EDGE,"E277"),sQuery(id+"F0.wireOp",EDGE,"E278"),sQuery(id+"F0.wireOp",EDGE,"E279"),sQuery(id+"F0.wireOp",EDGE,"E280"),sQuery(id+"F0.wireOp",EDGE,"E281"),sQuery(id+"F0.wireOp",EDGE,"E282"),sQuery(id+"F0.wireOp",EDGE,"E283"),sQuery(id+"F0.wireOp",EDGE,"E284"),sQuery(id+"F0.wireOp",EDGE,"E285"),sQuery(id+"F0.wireOp",EDGE,"E286"),sQuery(id+"F0.wireOp",EDGE,"E287"),sQuery(id+"F0.wireOp",EDGE,"E288"),sQuery(id+"F0.wireOp",EDGE,"E289"),sQuery(id+"F0.wireOp",EDGE,"E290"),sQuery(id+"F0.wireOp",EDGE,"E291"),sQuery(id+"F0.wireOp",EDGE,"E292"),sQuery(id+"F0.wireOp",EDGE,"E293"),sQuery(id+"F0.wireOp",EDGE,"E294"),sQuery(id+"F0.wireOp",EDGE,"E295"),sQuery(id+"F0.wireOp",EDGE,"E296"),sQuery(id+"F0.wireOp",EDGE,"E297"),sQuery(id+"F0.wireOp",EDGE,"E298"),sQuery(id+"F0.wireOp",EDGE,"E299"),sQuery(id+"F0.wireOp",EDGE,"E300"),sQuery(id+"F0.wireOp",EDGE,"E301"),sQuery(id+"F0.wireOp",EDGE,"E302"),sQuery(id+"F0.wireOp",EDGE,"E303"),sQuery(id+"F0.wireOp",EDGE,"E304"),sQuery(id+"F0.wireOp",EDGE,"E305"),sQuery(id+"F0.wireOp",EDGE,"E306"),sQuery(id+"F0.wireOp",EDGE,"E307"),sQuery(id+"F0.wireOp",EDGE,"E308"),sQuery(id+"F0.wireOp",EDGE,"E309"),sQuery(id+"F0.wireOp",EDGE,"E310"),sQuery(id+"F0.wireOp",EDGE,"E311"),sQuery(id+"F0.wireOp",EDGE,"E312"),sQuery(id+"F0.wireOp",EDGE,"E313"),sQuery(id+"F0.wireOp",EDGE,"E314"),sQuery(id+"F0.wireOp",EDGE,"E315"),sQuery(id+"F0.wireOp",EDGE,"E316"),sQuery(id+"F0.wireOp",EDGE,"E317"),sQuery(id+"F0.wireOp",EDGE,"E318"),sQuery(id+"F0.wireOp",EDGE,"E319"),sQuery(id+"F0.wireOp",EDGE,"E320"),sQuery(id+"F0.wireOp",EDGE,"E321"),sQuery(id+"F0.wireOp",EDGE,"E322"),sQuery(id+"F0.wireOp",EDGE,"E323"),sQuery(id+"F0.wireOp",EDGE,"E324"),sQuery(id+"F0.wireOp",EDGE,"E325"),sQuery(id+"F0.wireOp",EDGE,"E326"),sQuery(id+"F0.wireOp",EDGE,"E327"),sQuery(id+"F0.wireOp",EDGE,"E328"),sQuery(id+"F0.wireOp",EDGE,"E329"),sQuery(id+"F0.wireOp",EDGE,"E330"),sQuery(id+"F0.wireOp",EDGE,"E331"),sQuery(id+"F0.wireOp",EDGE,"E332"),sQuery(id+"F0.wireOp",EDGE,"E333"),sQuery(id+"F0.wireOp",EDGE,"E334"),sQuery(id+"F0.wireOp",EDGE,"E335"),sQuery(id+"F0.wireOp",EDGE,"E336"),sQuery(id+"F0.wireOp",EDGE,"E337"),sQuery(id+"F0.wireOp",EDGE,"E338"),sQuery(id+"F0.wireOp",EDGE,"E339"),sQuery(id+"F0.wireOp",EDGE,"E340"),sQuery(id+"F0.wireOp",EDGE,"E341"),sQuery(id+"F0.wireOp",EDGE,"E342"),sQuery(id+"F0.wireOp",EDGE,"E343"),sQuery(id+"F0.wireOp",EDGE,"E344"),sQuery(id+"F0.wireOp",EDGE,"E345"),sQuery(id+"F0.wireOp",EDGE,"E346"),sQuery(id+"F0.wireOp",EDGE,"E347"),sQuery(id+"F0.wireOp",EDGE,"E348"),sQuery(id+"F0.wireOp",EDGE,"E349"),sQuery(id+"F0.wireOp",EDGE,"E350"),sQuery(id+"F0.wireOp",EDGE,"E351"),sQuery(id+"F0.wireOp",EDGE,"E352"),sQuery(id+"F0.wireOp",EDGE,"E353"),sQuery(id+"F0.wireOp",EDGE,"E354"),sQuery(id+"F0.wireOp",EDGE,"E355"),sQuery(id+"F0.wireOp",EDGE,"E356"),sQuery(id+"F0.wireOp",EDGE,"E357"),sQuery(id+"F0.wireOp",EDGE,"E358"),sQuery(id+"F0.wireOp",EDGE,"E359"),sQuery(id+"F0.wireOp",EDGE,"E360"),sQuery(id+"F0.wireOp",EDGE,"E361"),sQuery(id+"F0.wireOp",EDGE,"E362"),sQuery(id+"F0.wireOp",EDGE,"E363"),sQuery(id+"F0.wireOp",EDGE,"E364"),sQuery(id+"F0.wireOp",EDGE,"E365"),sQuery(id+"F0.wireOp",EDGE,"E366"),sQuery(id+"F0.wireOp",EDGE,"E367"),sQuery(id+"F0.wireOp",EDGE,"E368"),sQuery(id+"F0.wireOp",EDGE,"E369"),sQuery(id+"F0.wireOp",EDGE,"E370"),sQuery(id+"F0.wireOp",EDGE,"E371"),sQuery(id+"F0.wireOp",EDGE,"E372"),sQuery(id+"F0.wireOp",EDGE,"E373"),sQuery(id+"F0.wireOp",EDGE,"E374"),sQuery(id+"F0.wireOp",EDGE,"E375"),sQuery(id+"F0.wireOp",EDGE,"E376"),sQuery(id+"F0.wireOp",EDGE,"E377"),sQuery(id+"F0.wireOp",EDGE,"E378"),sQuery(id+"F0.wireOp",EDGE,"E379"),sQuery(id+"F0.wireOp",EDGE,"E380"),sQuery(id+"F0.wireOp",EDGE,"E381"),sQuery(id+"F0.wireOp",EDGE,"E382"),sQuery(id+"F0.wireOp",EDGE,"E383"),sQuery(id+"F0.wireOp",EDGE,"E384"),sQuery(id+"F0.wireOp",EDGE,"E385"),sQuery(id+"F0.wireOp",EDGE,"E386"),sQuery(id+"F0.wireOp",EDGE,"E387"),sQuery(id+"F0.wireOp",EDGE,"E388"),sQuery(id+"F0.wireOp",EDGE,"E389"),sQuery(id+"F0.wireOp",EDGE,"E390"),sQuery(id+"F0.wireOp",EDGE,"E391"),sQuery(id+"F0.wireOp",EDGE,"E392"),sQuery(id+"F0.wireOp",EDGE,"E393"),sQuery(id+"F0.wireOp",EDGE,"E394"),sQuery(id+"F0.wireOp",EDGE,"E395"),sQuery(id+"F0.wireOp",EDGE,"E396"),sQuery(id+"F0.wireOp",EDGE,"E397"),sQuery(id+"F0.wireOp",EDGE,"E398"),sQuery(id+"F0.wireOp",EDGE,"E399"),sQuery(id+"F0.wireOp",EDGE,"E400"),sQuery(id+"F0.wireOp",EDGE,"E401"),sQuery(id+"F0.wireOp",EDGE,"E402"),sQuery(id+"F0.wireOp",EDGE,"E403"),sQuery(id+"F0.wireOp",EDGE,"E404"),sQuery(id+"F0.wireOp",EDGE,"E405"),sQuery(id+"F0.wireOp",EDGE,"E406"),sQuery(id+"F0.wireOp",EDGE,"E407"),sQuery(id+"F0.wireOp",EDGE,"E408"),sQuery(id+"F0.wireOp",EDGE,"E409"),sQuery(id+"F0.wireOp",EDGE,"E410"),sQuery(id+"F0.wireOp",EDGE,"E411"),sQuery(id+"F0.wireOp",EDGE,"E412"),sQuery(id+"F0.wireOp",EDGE,"E413"),sQuery(id+"F0.wireOp",EDGE,"E414"),sQuery(id+"F0.wireOp",EDGE,"E415"),sQuery(id+"F0.wireOp",EDGE,"E416"),sQuery(id+"F0.wireOp",EDGE,"E417"),sQuery(id+"F0.wireOp",EDGE,"E418"),sQuery(id+"F0.wireOp",EDGE,"E419"),sQuery(id+"F0.wireOp",EDGE,"E420"),sQuery(id+"F0.wireOp",EDGE,"E421"),sQuery(id+"F0.wireOp",EDGE,"E422"),sQuery(id+"F0.wireOp",EDGE,"E423"),sQuery(id+"F0.wireOp",EDGE,"E424"),sQuery(id+"F0.wireOp",EDGE,"E425"),sQuery(id+"F0.wireOp",EDGE,"E426"),sQuery(id+"F0.wireOp",EDGE,"E427"),sQuery(id+"F0.wireOp",EDGE,"E428"),sQuery(id+"F0.wireOp",EDGE,"E429"),sQuery(id+"F0.wireOp",EDGE,"E430"),sQuery(id+"F0.wireOp",EDGE,"E431"),sQuery(id+"F0.wireOp",EDGE,"E432"),sQuery(id+"F0.wireOp",EDGE,"E433"),sQuery(id+"F0.wireOp",EDGE,"E434"),sQuery(id+"F0.wireOp",EDGE,"E435"),sQuery(id+"F0.wireOp",EDGE,"E436"),sQuery(id+"F0.wireOp",EDGE,"E437"),sQuery(id+"F0.wireOp",EDGE,"E438"),sQuery(id+"F0.wireOp",EDGE,"E439"),sQuery(id+"F0.wireOp",EDGE,"E440"),sQuery(id+"F0.wireOp",EDGE,"E441"),sQuery(id+"F0.wireOp",EDGE,"E442"),sQuery(id+"F0.wireOp",EDGE,"E443"),sQuery(id+"F0.wireOp",EDGE,"E444"),sQuery(id+"F0.wireOp",EDGE,"E445"),sQuery(id+"F0.wireOp",EDGE,"E446"),sQuery(id+"F0.wireOp",EDGE,"E447"),sQuery(id+"F0.wireOp",EDGE,"E448"),sQuery(id+"F0.wireOp",EDGE,"E449"),sQuery(id+"F0.wireOp",EDGE,"E450"),sQuery(id+"F0.wireOp",EDGE,"E451"),sQuery(id+"F0.wireOp",EDGE,"E452"),sQuery(id+"F0.wireOp",EDGE,"E453"),sQuery(id+"F0.wireOp",EDGE,"E454"),sQuery(id+"F0.wireOp",EDGE,"E455"),sQuery(id+"F0.wireOp",EDGE,"E456"),sQuery(id+"F0.wireOp",EDGE,"E457"),sQuery(id+"F0.wireOp",EDGE,"E458"),sQuery(id+"F0.wireOp",EDGE,"E459"),sQuery(id+"F0.wireOp",EDGE,"E460"),sQuery(id+"F0.wireOp",EDGE,"E461"),sQuery(id+"F0.wireOp",EDGE,"E462"),sQuery(id+"F0.wireOp",EDGE,"E463"),sQuery(id+"F0.wireOp",EDGE,"E464"),sQuery(id+"F0.wireOp",EDGE,"E465"),sQuery(id+"F0.wireOp",EDGE,"E466"),sQuery(id+"F0.wireOp",EDGE,"E467"),sQuery(id+"F0.wireOp",EDGE,"E468"),sQuery(id+"F0.wireOp",EDGE,"E469"),sQuery(id+"F0.wireOp",EDGE,"E470"),sQuery(id+"F0.wireOp",EDGE,"E471"),sQuery(id+"F0.wireOp",EDGE,"E472"),sQuery(id+"F0.wireOp",EDGE,"E473"),sQuery(id+"F0.wireOp",EDGE,"E474"),sQuery(id+"F0.wireOp",EDGE,"E475")])],"isStart":true});
            fillet(context, id + "F3", {"entities" : qUnion([Q0]), "radius" : 0.5 * mm, "tangentPropagation" : true, "allowEdgeOverflow" : false});
        }
    });
